FREECAD ASSEMBLY — COMPONENT RECIPES ("feeder_assembly")

This assembly document has 52 components, labeled P0..P51 below (a component is one placed body or linked part). 40 of them carry a construction recipe — the FreeCAD feature program that regenerates the part from scratch, quoted from this document or its linked companion documents; the rest are supplied as boundary geometry only. No exploded tour is included for this assembly.
NOTE — document 3 of 3 of this assembly tour. The two overview renders and the header above are repeated from document 1; the component sections below continue where the previous document stopped.
COMPONENT P31 — recipe-attached ("Body027", modeled in this document).
Construction recipe (the document's own serialized feature program — sketch geometry with constraints, then the solid features built on it; lengths are millimeters unless a unit is written):

FEATURE [Sketcher::SketchObject] Sketch136
  FullyConstrained = true
  MapMode = 5
  Support = -> [XY_Plane026]
  sketch-geometry (5):
    g0: LineSegment StartX=0 StartY=0 StartZ=0 EndX=65 EndY=0 EndZ=0
    g1: LineSegment StartX=65 StartY=0 StartZ=0 EndX=65 EndY=4.27341 EndZ=0
    g2: ArcOfCircle CenterX=85 CenterY=75 CenterZ=0 NormalX=0 NormalY=0 NormalZ=1 AngleXU=0 Radius=73.5 StartAngle=3.80049 EndAngle=4.43681
    g3: LineSegment StartX=26.8859 StartY=30 StartZ=0 EndX=0 EndY=30 EndZ=0
    g4: LineSegment StartX=0 StartY=30 StartZ=0 EndX=0 EndY=0 EndZ=0
  constraints (16):
    c: Coincident(g0,g-1)
    c: PointOnObject(g0,g-1)
    c: Coincident(g1,g0)
    c: Vertical(g1)
    c: Coincident(g2,g1)
    c: Coincident(g3,g2)
    c: PointOnObject(g3,g-2)
    c: Horizontal(g3)
    c: Coincident(g4,g3)
    c: PointOnObject(g4,g-1)
    c: Vertical(g4)
    c: DistanceX(g2) = 85
    c: DistanceY(g2) = 75
    c: Diameter(g2) = 147
    c: DistanceX(g0,g0) = 65
    c: DistanceY(g3) = 30
FEATURE [PartDesign::Pad] Pad064
  Direction = (0,0,1)
  Length = 4
  Length2 = 10
  Profile = -> Sketch136
  ReferenceAxis = -> Sketch136 [N_Axis]
  Reversed = true
  Type = 0
FEATURE [Sketcher::SketchObject] Sketch137
  ExternalGeometry = -> [Pad064]
  FullyConstrained = true
  MapMode = 5
  Placement = pos=(0,0,0) rot=(1,0,0;1.5708rad)
  Support = -> [Pad064]
  sketch-geometry (4):
    g0: LineSegment StartX=65 StartY=-4 StartZ=0 EndX=0 EndY=-4 EndZ=0
    g1: LineSegment StartX=0 StartY=-4 StartZ=0 EndX=0 EndY=-20 EndZ=0
    g2: LineSegment StartX=0 StartY=-20 StartZ=0 EndX=65 EndY=-20 EndZ=0
    g3: LineSegment StartX=65 StartY=-20 StartZ=0 EndX=65 EndY=-4 EndZ=0
  constraints (11):
    c: Coincident(g0,g1)
    c: Coincident(g1,g2)
    c: Coincident(g2,g3)
    c: Coincident(g3,g0)
    c: Horizontal(g0)
    c: Horizontal(g2)
    c: Vertical(g1)
    c: Vertical(g3)
    c: Coincident(g0,g-3)
    c: PointOnObject(g1,g-2)
    c: DistanceY(g1) = -20
FEATURE [PartDesign::Pad] Pad065
  BaseFeature = -> Pad064
  Direction = (0,-1,2e-16)
  Length = 3
  Length2 = 10
  Profile = -> Sketch137
  ReferenceAxis = -> Sketch137 [N_Axis]
  Reversed = true
  Type = 0
FEATURE [Sketcher::SketchObject] Sketch138
  ExternalGeometry = -> [Pad065]
  FullyConstrained = true
  MapMode = 5
  Placement = pos=(0,0,0) rot=(0.57735,-0.57735,-0.57735;2.0944rad)
  Support = -> [Pad065]
  sketch-geometry (4):
    g0: LineSegment StartX=-30 StartY=-4 StartZ=0 EndX=-3 EndY=-4 EndZ=0
    g1: LineSegment StartX=-3 StartY=-4 StartZ=0 EndX=-3 EndY=-20 EndZ=0
    g2: LineSegment StartX=-3 StartY=-20 StartZ=0 EndX=-30 EndY=-20 EndZ=0
    g3: LineSegment StartX=-30 StartY=-20 StartZ=0 EndX=-30 EndY=-4 EndZ=0
  constraints (10):
    c: Coincident(g0,g1)
    c: Coincident(g1,g2)
    c: Coincident(g2,g3)
    c: Coincident(g3,g0)
    c: Horizontal(g0)
    c: Horizontal(g2)
    c: Vertical(g1)
    c: Vertical(g3)
    c: Coincident(g0,g-3)
    c: Coincident(g1,g-4)
FEATURE [PartDesign::Pad] Pad066
  BaseFeature = -> Pad065
  Direction = (-1,0,0)
  Length = 8
  Length2 = 10
  Profile = -> Sketch138
  ReferenceAxis = -> Sketch138 [N_Axis]
  Reversed = true
  Type = 0
FEATURE [Sketcher::SketchObject] Sketch139
  ExternalGeometry = -> [Pad066]
  FullyConstrained = true
  MapMode = 5
  Placement = pos=(8,0,0) rot=(0.57735,0.57735,0.57735;2.0944rad)
  Support = -> [Pad066]
  sketch-geometry (4):
    g0: ArcOfCircle CenterX=9 CenterY=-10 CenterZ=0 NormalX=0 NormalY=0 NormalZ=1 AngleXU=0 Radius=6 StartAngle=1.5708 EndAngle=4.71239
    g1: ArcOfCircle CenterX=21 CenterY=-10 CenterZ=0 NormalX=0 NormalY=0 NormalZ=1 AngleXU=0 Radius=6 StartAngle=4.71239 EndAngle=7.85398
    g2: LineSegment StartX=9 StartY=-16 StartZ=0 EndX=21 EndY=-16 EndZ=0
    g3: LineSegment StartX=21 StartY=-4 StartZ=0 EndX=9 EndY=-4 EndZ=0
  constraints (10):
    c: Tangent(g0,g2) = -1.5708
    c: Tangent(g2,g1) = -1.5708
    c: Tangent(g1,g3) = -1.5708
    c: Tangent(g3,g0) = -1.5708
    c: Equal(g0,g1)
    c: Horizontal(g2)
    c: Diameter(g1) = 12
    c: DistanceY(g-4,g0) = 10
    c: DistanceX(g1,g-3) = 9
    c: DistanceX(g0) = 9
FEATURE [PartDesign::Pocket] Pocket067
  BaseFeature = -> Pad066
  Direction = (-1,0,0)
  Length = 5
  Length2 = 5
  Profile = -> Sketch139
  ReferenceAxis = -> Sketch139 [N_Axis]
  Type = 0
FEATURE [PartDesign::Fillet] Fillet060
  Base = -> Pocket067 [Edge28]
  BaseFeature = -> Pocket067
  Radius = 1
  SupportTransform = false
  UseAllEdges = false
FEATURE [PartDesign::Fillet] Fillet061
  Base = -> Fillet060 [Edge48]
  BaseFeature = -> Fillet060
  Radius = 10
  SupportTransform = false
  UseAllEdges = false
FEATURE [PartDesign::Fillet] Fillet062
  Base = -> Fillet061 [Edge56]
  BaseFeature = -> Fillet061
  Radius = 3.5
  SupportTransform = false
  UseAllEdges = false
FEATURE [PartDesign::Fillet] Fillet063
  Base = -> Fillet062 [Edge32,Edge25,Edge47,Edge23,Edge26,Edge24,Edge1,Edge2,Edge20,Edge11]
  BaseFeature = -> Fillet062
  Radius = 1
  SupportTransform = false
  UseAllEdges = false
FEATURE [PartDesign::Fillet] Fillet064
  Base = -> Fillet063 [Face31,Face32,Face21]
  BaseFeature = -> Fillet063
  Radius = 1
  SupportTransform = false
  UseAllEdges = false
FEATURE [PartDesign::Fillet] Fillet065
  Base = -> Fillet064 [Face33]
  BaseFeature = -> Fillet064
  Radius = 0.5
  SupportTransform = false
  UseAllEdges = false
FEATURE [PartDesign::Fillet] Fillet066
  Base = -> Fillet065 [Face23]
  BaseFeature = -> Fillet065
  Radius = 0.9
  SupportTransform = false
  UseAllEdges = false
FEATURE [Sketcher::SketchObject] Sketch140
  ExternalGeometry = -> [Fillet066]
  FullyConstrained = true
  MapMode = 5
  Placement = pos=(3,0,0) rot=(0.57735,0.57735,0.57735;2.0944rad)
  Support = -> [Fillet066]
  sketch-geometry (2):
    g0: Circle CenterX=9 CenterY=-10 CenterZ=0 NormalX=0 NormalY=0 NormalZ=1 AngleXU=0 Radius=2.075
    g1: Circle CenterX=21 CenterY=-10 CenterZ=0 NormalX=0 NormalY=0 NormalZ=1 AngleXU=0 Radius=2.075
  constraints (4):
    c: Coincident(g0,g-3)
    c: Coincident(g1,g-4)
    c: Equal(g0,g1)
    c: Diameter(g1) = 4.15
FEATURE [PartDesign::Pocket] Pocket068
  BaseFeature = -> Fillet066
  Direction = (-1,0,0)
  Length = 5
  Length2 = 5
  Profile = -> Sketch140
  ReferenceAxis = -> Sketch140 [N_Axis]
  Type = 0
FEATURE [Sketcher::SketchObject] Sketch141
  ExternalGeometry = -> [Pocket068]
  FullyConstrained = true
  MapMode = 5
  Placement = pos=(0,3,-7e-16) rot=(0,0.707107,0.707107;3.14159rad)
  Support = -> [Pocket068]
  sketch-geometry (4):
    g0: LineSegment StartX=-8 StartY=-18.5 StartZ=0 EndX=-38 EndY=-18.5 EndZ=0
    g1: LineSegment StartX=-38 StartY=-18.5 StartZ=0 EndX=-38 EndY=-16.5 EndZ=0
    g2: LineSegment StartX=-38 StartY=-16.5 StartZ=0 EndX=-8 EndY=-16.5 EndZ=0
    g3: LineSegment StartX=-8 StartY=-16.5 StartZ=0 EndX=-8 EndY=-18.5 EndZ=0
  constraints (12):
    c: Coincident(g0,g1)
    c: Coincident(g1,g2)
    c: Coincident(g2,g3)
    c: Coincident(g3,g0)
    c: Horizontal(g0)
    c: Horizontal(g2)
    c: Vertical(g1)
    c: Vertical(g3)
    c: DistanceY(g3,g3) = 2
    c: DistanceX(g0,g0) = 30
    c: PointOnObject(g0,g-3)
    c: DistanceY(g-3,g0) = 0.5
FEATURE [PartDesign::Pad] Pad067
  BaseFeature = -> Pocket068
  Direction = (0,1,-2e-16)
  Length = 5
  Length2 = 10
  Profile = -> Sketch141
  ReferenceAxis = -> Sketch141 [N_Axis]
  Type = 0
FEATURE [Sketcher::SketchObject] Sketch142
  ExternalGeometry = -> [Pad067]
  FullyConstrained = true
  MapMode = 5
  Placement = pos=(0,-4.1e-15,-18.5) rot=(1,0,0;3.14159rad)
  Support = -> [Pad067]
  sketch-geometry (3):
    g0: LineSegment StartX=8 StartY=-8 StartZ=0 EndX=38 EndY=-3 EndZ=0
    g1: LineSegment StartX=38 StartY=-3 StartZ=0 EndX=38 EndY=-8 EndZ=0
    g2: LineSegment StartX=38 StartY=-8 StartZ=0 EndX=8 EndY=-8 EndZ=0
  constraints (6):
    c: Coincident(g0,g-6)
    c: Coincident(g0,g-5)
    c: Coincident(g1,g0)
    c: Coincident(g1,g-5)
    c: Coincident(g2,g1)
    c: Coincident(g2,g0)
FEATURE [PartDesign::Pocket] Pocket069
  BaseFeature = -> Pad067
  Direction = (0,2e-16,1)
  Length = 0
  Length2 = 5
  Profile = -> Sketch142
  ReferenceAxis = -> Sketch142 [N_Axis]
  Type = 2
FEATURE [PartDesign::Fillet] Fillet067
  Base = -> Pocket069 [Face26,Face27,Face24]
  BaseFeature = -> Pocket069
  Radius = 0.4
  SupportTransform = false
  UseAllEdges = false
FEATURE [PartDesign::Fillet] Fillet068
  Base = -> Fillet067 [Face69,Face68]
  BaseFeature = -> Fillet067
  Radius = 0.3
  SupportTransform = false
  UseAllEdges = false
FEATURE [PartDesign::Body] Body027
  Group = -> [Sketch136,Pad064,Sketch137,Pad065,Sketch138,Pad066,Sketch139,Pocket067,Fillet060,Fillet061,Fillet062,Fillet063,Fillet064,Fillet065,Fillet066,Sketch140,Pocket068,Sketch141,Pad067,Sketch142,Pocket069,Fillet067,Fillet068]
  Origin = -> Origin026
  Tip = -> Fillet068
COMPONENT P32 — recipe-attached ("Body029", modeled in this document).
Construction recipe (the document's own serialized feature program — sketch geometry with constraints, then the solid features built on it; lengths are millimeters unless a unit is written):

FEATURE [Sketcher::SketchObject] Sketch144
  FullyConstrained = true
  MapMode = 5
  Support = -> [XY_Plane028]
  sketch-geometry (4):
    g0: LineSegment StartX=0 StartY=0 StartZ=0 EndX=65.5 EndY=0 EndZ=0
    g1: LineSegment StartX=65.5 StartY=0 StartZ=0 EndX=65.5 EndY=30.6 EndZ=0
    g2: LineSegment StartX=65.5 StartY=30.6 StartZ=0 EndX=0 EndY=30.6 EndZ=0
    g3: LineSegment StartX=0 StartY=30.6 StartZ=0 EndX=0 EndY=0 EndZ=0
  constraints (11):
    c: Coincident(g0,g1)
    c: Coincident(g1,g2)
    c: Coincident(g2,g3)
    c: Coincident(g3,g0)
    c: Horizontal(g0)
    c: Horizontal(g2)
    c: Vertical(g1)
    c: Vertical(g3)
    c: Coincident(g0,g-1)
    c: DistanceX(g0,g0) = 65.5
    c: DistanceY(g1,g1) = 30.6
FEATURE [PartDesign::Pad] Pad069
  Direction = (0,0,1)
  Length = 1.6
  Length2 = 10
  Profile = -> Sketch144
  ReferenceAxis = -> Sketch144 [N_Axis]
  Type = 0
FEATURE [Sketcher::SketchObject] Sketch145
  ExternalGeometry = -> [Pad069]
  FullyConstrained = true
  MapMode = 5
  Placement = pos=(0,0,1.6) rot=(0,0,1;0rad)
  Support = -> [Pad069]
  sketch-geometry (4):
    g0: Circle CenterX=3.5 CenterY=26.5 CenterZ=0 NormalX=0 NormalY=0 NormalZ=1 AngleXU=0 Radius=1.5
    g1: Circle CenterX=3.5 CenterY=3.5 CenterZ=0 NormalX=0 NormalY=0 NormalZ=1 AngleXU=0 Radius=1.5
    g2: Circle CenterX=61.5 CenterY=3.5 CenterZ=0 NormalX=0 NormalY=0 NormalZ=1 AngleXU=0 Radius=1.5
    g3: Circle CenterX=61.5 CenterY=26.5 CenterZ=0 NormalX=0 NormalY=0 NormalZ=1 AngleXU=0 Radius=1.5
  constraints (12):
    c: Equal(g2,g3)
    c: Equal(g3,g0)
    c: Equal(g0,g1)
    c: Diameter(g2) = 3
    c: Horizontal(g1,g2)
    c: Horizontal(g3,g0)
    c: Vertical(g3,g2)
    c: Vertical(g0,g1)
    c: DistanceX(g1) = 3.5
    c: DistanceY(g1) = 3.5
    c: DistanceX(g1,g2) = 58
    c: DistanceY(g1,g0) = 23
FEATURE [PartDesign::Pocket] Pocket070
  BaseFeature = -> Pad069
  Direction = (0,0,-1)
  Length = 5
  Length2 = 5
  Profile = -> Sketch145
  ReferenceAxis = -> Sketch145 [N_Axis]
  Type = 0
FEATURE [Sketcher::SketchObject] Sketch146
  ExternalGeometry = -> [Pocket070]
  FullyConstrained = true
  MapMode = 5
  Placement = pos=(0,0,0) rot=(1,0,0;3.14159rad)
  Support = -> [Pocket070]
  sketch-geometry (6):
    g0: LineSegment StartX=6.875 StartY=-29 StartZ=0 EndX=58.125 EndY=-29 EndZ=0
    g1: LineSegment StartX=58.125 StartY=-29 StartZ=0 EndX=58.125 EndY=-24 EndZ=0
    g2: LineSegment StartX=58.125 StartY=-24 StartZ=0 EndX=6.875 EndY=-24 EndZ=0
    g3: LineSegment StartX=6.875 StartY=-24 StartZ=0 EndX=6.875 EndY=-29 EndZ=0
    g4: GeomPoint X=32.5 Y=-29 Z=0
    g5: GeomPoint X=6.875 Y=-26.5 Z=0
  constraints (14):
    c: Coincident(g0,g1)
    c: Coincident(g1,g2)
    c: Coincident(g2,g3)
    c: Coincident(g3,g0)
    c: Horizontal(g0)
    c: Horizontal(g2)
    c: Vertical(g1)
    c: Vertical(g3)
    c: DistanceX(g0,g0) = 51.25
    c: DistanceY(g3,g3) = 5
    c: Symmetric(g0,g0,g4)
    c: DistanceX(g-4,g4) = 29
    c: Symmetric(g3,g3,g5)
    c: Horizontal(g5,g-4)
FEATURE [PartDesign::Pad] Pad070
  BaseFeature = -> Pocket070
  Direction = (0,0,-1)
  Length = 30
  Length2 = 10
  Profile = -> Sketch146
  ReferenceAxis = -> Sketch146 [N_Axis]
  Type = 0
FEATURE [Sketcher::SketchObject] Sketch147
  ExternalGeometry = -> [Pad070]
  FullyConstrained = true
  MapMode = 5
  Placement = pos=(0,0,1.6) rot=(0,0,1;0rad)
  Support = -> [Pad070]
  sketch-geometry (10):
    g0: LineSegment StartX=6.5 StartY=30.6 StartZ=0 EndX=58.5 EndY=30.6 EndZ=0
    g1: LineSegment StartX=58.5 StartY=30.6 StartZ=0 EndX=58.5 EndY=24.1 EndZ=0
    g2: LineSegment StartX=58.5 StartY=24.1 StartZ=0 EndX=6.5 EndY=24.1 EndZ=0
    g3: LineSegment StartX=6.5 StartY=24.1 StartZ=0 EndX=6.5 EndY=30.6 EndZ=0
    g4: LineSegment StartX=8.5 StartY=0 StartZ=0 EndX=56.5 EndY=0 EndZ=0
    g5: LineSegment StartX=56.5 StartY=0 StartZ=0 EndX=56.5 EndY=8.5 EndZ=0
    g6: LineSegment StartX=56.5 StartY=8.5 StartZ=0 EndX=8.5 EndY=8.5 EndZ=0
    g7: LineSegment StartX=8.5 StartY=8.5 StartZ=0 EndX=8.5 EndY=0 EndZ=0
    g8: GeomPoint X=32.5 Y=8.5 Z=0
    g9: GeomPoint X=32.5 Y=24.1 Z=0
  constraints (26):
    c: Coincident(g0,g1)
    c: Coincident(g1,g2)
    c: Coincident(g2,g3)
    c: Coincident(g3,g0)
    c: Horizontal(g0)
    c: Horizontal(g2)
    c: Vertical(g1)
    c: Vertical(g3)
    c: PointOnObject(g0,g-3)
    c: Coincident(g4,g5)
    c: Coincident(g5,g6)
    c: Coincident(g6,g7)
    c: Coincident(g7,g4)
    c: Horizontal(g4)
    c: Horizontal(g6)
    c: Vertical(g5)
    c: Vertical(g7)
    c: PointOnObject(g4,g-1)
    c: DistanceY(g5,g5) = 8.5
    c: DistanceX(g4,g4) = 48
    c: DistanceX(g2,g2) = 52
    c: DistanceY(g1,g1) = 6.5
    c: Symmetric(g6,g6,g8)
    c: Symmetric(g2,g2,g9)
    c: Vertical(g9,g8)
    c: DistanceX(g-4,g9) = 29
FEATURE [PartDesign::Pad] Pad071
  BaseFeature = -> Pad070
  Direction = (0,0,1)
  Length = 20
  Length2 = 10
  Profile = -> Sketch147
  ReferenceAxis = -> Sketch147 [N_Axis]
  Type = 0
FEATURE [Sketcher::SketchObject] Sketch148
  FullyConstrained = true
  MapMode = 5
  Placement = pos=(0,0,1.6) rot=(0,0,1;0rad)
  Support = -> [Pad071]
  sketch-geometry (4):
    g0: LineSegment StartX=0 StartY=11.5 StartZ=0 EndX=7.5 EndY=11.5 EndZ=0
    g1: LineSegment StartX=7.5 StartY=11.5 StartZ=0 EndX=7.5 EndY=18.5 EndZ=0
    g2: LineSegment StartX=7.5 StartY=18.5 StartZ=0 EndX=0 EndY=18.5 EndZ=0
    g3: LineSegment StartX=0 StartY=18.5 StartZ=0 EndX=0 EndY=11.5 EndZ=0
  constraints (12):
    c: Coincident(g0,g1)
    c: Coincident(g1,g2)
    c: Coincident(g2,g3)
    c: Coincident(g3,g0)
    c: Horizontal(g0)
    c: Horizontal(g2)
    c: Vertical(g1)
    c: Vertical(g3)
    c: PointOnObject(g0,g-2)
    c: DistanceY(g0) = 11.5
    c: DistanceY(g1,g1) = 7
    c: DistanceX(g0,g0) = 7.5
FEATURE [PartDesign::Pad] Pad072
  BaseFeature = -> Pad071
  Direction = (0,0,1)
  Length = 9.5
  Length2 = 10
  Profile = -> Sketch148
  ReferenceAxis = -> Sketch148 [N_Axis]
  Type = 0
FEATURE [PartDesign::Body] Body029
  Group = -> [Sketch144,Pad069,Sketch145,Pocket070,Sketch146,Pad070,Sketch147,Pad071,Sketch148,Pad072]
  Origin = -> Origin028
  Tip = -> Pad072
COMPONENT P33 — recipe-attached ("Body030", modeled in this document).
Construction recipe (the document's own serialized feature program — sketch geometry with constraints, then the solid features built on it; lengths are millimeters unless a unit is written):

FEATURE [Sketcher::SketchObject] Sketch149
  FullyConstrained = true
  MapMode = 5
  Support = -> [XY_Plane029]
  sketch-geometry (4):
    g0: LineSegment StartX=0 StartY=0 StartZ=0 EndX=85 EndY=0 EndZ=0
    g1: LineSegment StartX=85 StartY=0 StartZ=0 EndX=85 EndY=56 EndZ=0
    g2: LineSegment StartX=85 StartY=56 StartZ=0 EndX=0 EndY=56 EndZ=0
    g3: LineSegment StartX=0 StartY=56 StartZ=0 EndX=0 EndY=0 EndZ=0
  constraints (11):
    c: Coincident(g0,g1)
    c: Coincident(g1,g2)
    c: Coincident(g2,g3)
    c: Coincident(g3,g0)
    c: Horizontal(g0)
    c: Horizontal(g2)
    c: Vertical(g1)
    c: Vertical(g3)
    c: Coincident(g0,g-1)
    c: DistanceX(g0,g0) = 85
    c: DistanceY(g3,g3) = 56
FEATURE [PartDesign::Pad] Pad073
  Direction = (0,0,1)
  Length = 1.5
  Length2 = 10
  Profile = -> Sketch149
  ReferenceAxis = -> Sketch149 [N_Axis]
  Type = 0
FEATURE [Sketcher::SketchObject] Sketch150
  ExternalGeometry = -> [Pad073]
  FullyConstrained = true
  MapMode = 5
  Placement = pos=(0,0,1.5) rot=(0,0,1;0rad)
  Support = -> [Pad073]
  sketch-geometry (4):
    g0: Circle CenterX=3.5 CenterY=52.5 CenterZ=0 NormalX=0 NormalY=0 NormalZ=1 AngleXU=0 Radius=1.375
    g1: Circle CenterX=61.5 CenterY=52.5 CenterZ=0 NormalX=0 NormalY=0 NormalZ=1 AngleXU=0 Radius=1.375
    g2: Circle CenterX=3.5 CenterY=3.5 CenterZ=0 NormalX=0 NormalY=0 NormalZ=1 AngleXU=0 Radius=1.375
    g3: Circle CenterX=61.5 CenterY=3.5 CenterZ=0 NormalX=0 NormalY=0 NormalZ=1 AngleXU=0 Radius=1.375
  constraints (12):
    c: Equal(g0,g1)
    c: Equal(g1,g2)
    c: Equal(g2,g3)
    c: Diameter(g1) = 2.75
    c: Vertical(g0,g2)
    c: DistanceX(g2) = 3.5
    c: DistanceY(g2) = 3.5
    c: DistanceY(g0,g-3) = 3.5
    c: Horizontal(g3,g2)
    c: Horizontal(g1,g0)
    c: DistanceX(g0,g1) = 58
    c: Vertical(g3,g1)
FEATURE [PartDesign::Pocket] Pocket071
  BaseFeature = -> Pad073
  Direction = (0,0,-1)
  Length = 5
  Length2 = 5
  Profile = -> Sketch150
  ReferenceAxis = -> Sketch150 [N_Axis]
  Type = 0
FEATURE [Sketcher::SketchObject] Sketch151
  FullyConstrained = true
  MapMode = 5
  Placement = pos=(0,0,1.5) rot=(0,0,1;0rad)
  Support = -> [Pocket071]
  sketch-geometry (5):
    g0: LineSegment StartX=24.5 StartY=-1.5 StartZ=0 EndX=39.5 EndY=-1.5 EndZ=0
    g1: LineSegment StartX=39.5 StartY=-1.5 StartZ=0 EndX=39.5 EndY=10 EndZ=0
    g2: LineSegment StartX=39.5 StartY=10 StartZ=0 EndX=24.5 EndY=10 EndZ=0
    g3: LineSegment StartX=24.5 StartY=10 StartZ=0 EndX=24.5 EndY=-1.5 EndZ=0
    g4: GeomPoint X=32 Y=-1.5 Z=0
  constraints (13):
    c: Coincident(g0,g1)
    c: Coincident(g1,g2)
    c: Coincident(g2,g3)
    c: Coincident(g3,g0)
    c: Horizontal(g0)
    c: Horizontal(g2)
    c: Vertical(g1)
    c: Vertical(g3)
    c: DistanceX(g0,g0) = 15
    c: DistanceY(g1,g1) = 11.5
    c: DistanceY(g0) = -1.5
    c: Symmetric(g0,g0,g4)
    c: DistanceX(g4) = 32
FEATURE [PartDesign::Pad] Pad074
  BaseFeature = -> Pocket071
  Direction = (0,0,1)
  Length = 6.5
  Length2 = 0.5
  Profile = -> Sketch151
  ReferenceAxis = -> Sketch151 [N_Axis]
  Type = 0
FEATURE [Sketcher::SketchObject] Sketch152
  ExternalGeometry = -> [Pad074]
  FullyConstrained = true
  MapMode = 5
  Placement = pos=(0,0,1.5) rot=(0,0,1;0rad)
  Support = -> [Pad074]
  sketch-geometry (10):
    g0: LineSegment StartX=69.5 StartY=21.5 StartZ=0 EndX=87 EndY=21.5 EndZ=0
    g1: LineSegment StartX=87 StartY=21.5 StartZ=0 EndX=87 EndY=36.5 EndZ=0
    g2: LineSegment StartX=87 StartY=36.5 StartZ=0 EndX=69.5 EndY=36.5 EndZ=0
    g3: LineSegment StartX=69.5 StartY=36.5 StartZ=0 EndX=69.5 EndY=21.5 EndZ=0
    g4: LineSegment StartX=69.5 StartY=39.5 StartZ=0 EndX=87 EndY=39.5 EndZ=0
    g5: LineSegment StartX=87 StartY=39.5 StartZ=0 EndX=87 EndY=54.5 EndZ=0
    g6: LineSegment StartX=87 StartY=54.5 StartZ=0 EndX=69.5 EndY=54.5 EndZ=0
    g7: LineSegment StartX=69.5 StartY=54.5 StartZ=0 EndX=69.5 EndY=39.5 EndZ=0
    g8: GeomPoint X=87 Y=29 Z=0
    g9: GeomPoint X=87 Y=47 Z=0
  constraints (26):
    c: Coincident(g0,g1)
    c: Coincident(g1,g2)
    c: Coincident(g2,g3)
    c: Coincident(g3,g0)
    c: Horizontal(g0)
    c: Horizontal(g2)
    c: Vertical(g1)
    c: Vertical(g3)
    c: Coincident(g4,g5)
    c: Coincident(g5,g6)
    c: Coincident(g6,g7)
    c: Coincident(g7,g4)
    c: Horizontal(g4)
    c: Horizontal(g6)
    c: Vertical(g5)
    c: Vertical(g7)
    c: Equal(g5,g1)
    c: Equal(g0,g4)
    c: Vertical(g0,g4)
    c: Symmetric(g5,g5,g9)
    c: Symmetric(g1,g1,g8)
    c: DistanceY(g5,g5) = 15
    c: DistanceY(g9) = 47
    c: DistanceY(g8) = 29
    c: DistanceX(g-3,g0) = 2
    c: DistanceX(g0,g0) = 17.5
FEATURE [PartDesign::Pad] Pad075
  BaseFeature = -> Pad074
  Direction = (0,0,1)
  Length = 16
  Length2 = 10
  Profile = -> Sketch152
  ReferenceAxis = -> Sketch152 [N_Axis]
  Type = 0
FEATURE [Sketcher::SketchObject] Sketch153
  ExternalGeometry = -> [Pad075]
  FullyConstrained = true
  MapMode = 5
  Placement = pos=(0,0,1.5) rot=(0,0,1;0rad)
  Support = -> [Pad075]
  sketch-geometry (5):
    g0: LineSegment StartX=65.5 StartY=2.25 StartZ=0 EndX=87 EndY=2.25 EndZ=0
    g1: LineSegment StartX=87 StartY=2.25 StartZ=0 EndX=87 EndY=18.25 EndZ=0
    g2: LineSegment StartX=87 StartY=18.25 StartZ=0 EndX=65.5 EndY=18.25 EndZ=0
    g3: LineSegment StartX=65.5 StartY=18.25 StartZ=0 EndX=65.5 EndY=2.25 EndZ=0
    g4: GeomPoint X=87 Y=10.25 Z=0
  constraints (13):
    c: Coincident(g0,g1)
    c: Coincident(g1,g2)
    c: Coincident(g2,g3)
    c: Coincident(g3,g0)
    c: Horizontal(g0)
    c: Horizontal(g2)
    c: Vertical(g1)
    c: Vertical(g3)
    c: DistanceY(g1,g1) = 16
    c: DistanceX(g0,g0) = 21.5
    c: DistanceX(g-3,g0) = 2
    c: Symmetric(g1,g1,g4)
    c: DistanceY(g4) = 10.25
FEATURE [PartDesign::Pad] Pad076
  BaseFeature = -> Pad075
  Direction = (0,0,1)
  Length = 13.5
  Length2 = 10
  Profile = -> Sketch153
  ReferenceAxis = -> Sketch153 [N_Axis]
  Type = 0
FEATURE [Sketcher::SketchObject] Sketch154
  ExternalGeometry = -> [Pad076]
  FullyConstrained = true
  MapMode = 5
  Placement = pos=(0,0,1.5) rot=(0,0,1;0rad)
  Support = -> [Pad076]
  sketch-geometry (6):
    g0: LineSegment StartX=7.5 StartY=50 StartZ=0 EndX=57.5 EndY=50 EndZ=0
    g1: LineSegment StartX=57.5 StartY=50 StartZ=0 EndX=57.5 EndY=55 EndZ=0
    g2: LineSegment StartX=57.5 StartY=55 StartZ=0 EndX=7.5 EndY=55 EndZ=0
    g3: LineSegment StartX=7.5 StartY=55 StartZ=0 EndX=7.5 EndY=50 EndZ=0
    g4: GeomPoint X=32.5 Y=55 Z=0
    g5: GeomPoint X=7.5 Y=52.5 Z=0
  constraints (14):
    c: Coincident(g0,g1)
    c: Coincident(g1,g2)
    c: Coincident(g2,g3)
    c: Coincident(g3,g0)
    c: Horizontal(g0)
    c: Horizontal(g2)
    c: Vertical(g1)
    c: Vertical(g3)
    c: Symmetric(g2,g2,g4)
    c: DistanceX(g-3,g4) = 29
    c: DistanceY(g3,g3) = 5
    c: DistanceX(g0,g0) = 50
    c: Symmetric(g3,g3,g5)
    c: Horizontal(g5,g-3)
FEATURE [PartDesign::Pad] Pad077
  BaseFeature = -> Pad076
  Direction = (0,0,1)
  Length = 30
  Length2 = 10
  Profile = -> Sketch154
  ReferenceAxis = -> Sketch154 [N_Axis]
  Type = 0
FEATURE [Sketcher::SketchObject] Sketch155
  FullyConstrained = true
  MapMode = 5
  Placement = pos=(0,0,1.5) rot=(0,0,1;0rad)
  Support = -> [Pad077]
  sketch-geometry (5):
    g0: LineSegment StartX=6.6 StartY=4.5 StartZ=0 EndX=14.6 EndY=4.5 EndZ=0
    g1: LineSegment StartX=14.6 StartY=4.5 StartZ=0 EndX=14.6 EndY=-1.5 EndZ=0
    g2: LineSegment StartX=14.6 StartY=-1.5 StartZ=0 EndX=6.6 EndY=-1.5 EndZ=0
    g3: LineSegment StartX=6.6 StartY=-1.5 StartZ=0 EndX=6.6 EndY=4.5 EndZ=0
    g4: GeomPoint X=10.6 Y=-1.5 Z=0
  constraints (13):
    c: Coincident(g0,g1)
    c: Coincident(g1,g2)
    c: Coincident(g2,g3)
    c: Coincident(g3,g0)
    c: Horizontal(g0)
    c: Horizontal(g2)
    c: Vertical(g1)
    c: Vertical(g3)
    c: DistanceX(g2,g2) = 8
    c: DistanceY(g3,g3) = 6
    c: DistanceY(g2) = -1.5
    c: Symmetric(g2,g2,g4)
    c: DistanceX(g4) = 10.6
FEATURE [PartDesign::Pad] Pad078
  BaseFeature = -> Pad077
  Direction = (0,0,1)
  Length = 3
  Length2 = 0.5
  Profile = -> Sketch155
  ReferenceAxis = -> Sketch155 [N_Axis]
  Type = 4
FEATURE [Sketcher::SketchObject] Sketch156
  FullyConstrained = true
  MapMode = 5
  Placement = pos=(0,0,1.5) rot=(0,0,1;0rad)
  Support = -> [Pad078]
  sketch-geometry (5):
    g0: LineSegment StartX=49.875 StartY=12.5 StartZ=0 EndX=57.125 EndY=12.5 EndZ=0
    g1: LineSegment StartX=57.125 StartY=12.5 StartZ=0 EndX=57.125 EndY=-2.5 EndZ=0
    g2: LineSegment StartX=57.125 StartY=-2.5 StartZ=0 EndX=49.875 EndY=-2.5 EndZ=0
    g3: LineSegment StartX=49.875 StartY=-2.5 StartZ=0 EndX=49.875 EndY=12.5 EndZ=0
    g4: GeomPoint X=53.5 Y=-2.5 Z=0
  constraints (13):
    c: Coincident(g0,g1)
    c: Coincident(g1,g2)
    c: Coincident(g2,g3)
    c: Coincident(g3,g0)
    c: Horizontal(g0)
    c: Horizontal(g2)
    c: Vertical(g1)
    c: Vertical(g3)
    c: DistanceX(g2,g2) = 7.25
    c: Symmetric(g2,g2,g4)
    c: DistanceX(g4) = 53.5
    c: DistanceY(g1,g1) = 15
    c: DistanceY(g4) = -2.5
FEATURE [PartDesign::Pad] Pad079
  BaseFeature = -> Pad078
  Direction = (0,0,1)
  Length = 6
  Length2 = 10
  Profile = -> Sketch156
  ReferenceAxis = -> Sketch156 [N_Axis]
  Type = 0
FEATURE [Sketcher::SketchObject] Sketch157
  FullyConstrained = true
  MapMode = 5
  Placement = pos=(0,0,0) rot=(1,0,0;3.14159rad)
  Support = -> [Pad079]
  sketch-geometry (4):
    g0: LineSegment StartX=-3 StartY=-22 StartZ=0 EndX=12.8 EndY=-22 EndZ=0
    g1: LineSegment StartX=12.8 StartY=-22 StartZ=0 EndX=12.8 EndY=-34 EndZ=0
    g2: LineSegment StartX=12.8 StartY=-34 StartZ=0 EndX=-3 EndY=-34 EndZ=0
    g3: LineSegment StartX=-3 StartY=-34 StartZ=0 EndX=-3 EndY=-22 EndZ=0
  constraints (12):
    c: Coincident(g0,g1)
    c: Coincident(g1,g2)
    c: Coincident(g2,g3)
    c: Coincident(g3,g0)
    c: Horizontal(g0)
    c: Horizontal(g2)
    c: Vertical(g1)
    c: Vertical(g3)
    c: DistanceX(g2,g2) = 15.8
    c: DistanceY(g1,g1) = 12
    c: DistanceY(g0) = -22
    c: DistanceX(g0) = -3
FEATURE [PartDesign::Pad] Pad080
  BaseFeature = -> Pad079
  Direction = (0,0,-1)
  Length = 1.5
  Length2 = 10
  Profile = -> Sketch157
  ReferenceAxis = -> Sketch157 [N_Axis]
  Type = 0
FEATURE [Sketcher::SketchObject] Sketch158
  FullyConstrained = true
  MapMode = 5
  Placement = pos=(0,0,0) rot=(1,0,0;3.14159rad)
  Support = -> [Pad080]
  sketch-geometry (4):
    g0: LineSegment StartX=17 StartY=-10 StartZ=0 EndX=82 EndY=-10 EndZ=0
    g1: LineSegment StartX=82 StartY=-10 StartZ=0 EndX=82 EndY=-45 EndZ=0
    g2: LineSegment StartX=82 StartY=-45 StartZ=0 EndX=17 EndY=-45 EndZ=0
    g3: LineSegment StartX=17 StartY=-45 StartZ=0 EndX=17 EndY=-10 EndZ=0
  constraints (12):
    c: Coincident(g0,g1)
    c: Coincident(g1,g2)
    c: Coincident(g2,g3)
    c: Coincident(g3,g0)
    c: Horizontal(g0)
    c: Horizontal(g2)
    c: Vertical(g1)
    c: Vertical(g3)
    c: DistanceX(g0) = 17
    c: DistanceY(g0) = -10
    c: DistanceY(g1,g1) = 35
    c: DistanceX(g2,g2) = 65
FEATURE [PartDesign::Pad] Pad081
  BaseFeature = -> Pad080
  Direction = (0,0,-1)
  Length = 2.2
  Length2 = 10
  Profile = -> Sketch158
  ReferenceAxis = -> Sketch158 [N_Axis]
  Type = 0
FEATURE [PartDesign::Body] Body030
  Group = -> [Sketch149,Pad073,Sketch150,Pocket071,Sketch151,Pad074,Sketch152,Pad075,Sketch153,Pad076,Sketch154,Pad077,Sketch155,Pad078,Sketch156,Pad079,Sketch157,Pad080,Sketch158,Pad081]
  Origin = -> Origin029
  Tip = -> Pad081
COMPONENT P34 — recipe-attached ("Body031", modeled in this document).
Construction recipe (the document's own serialized feature program — sketch geometry with constraints, then the solid features built on it; lengths are millimeters unless a unit is written):

FEATURE [Sketcher::SketchObject] Sketch159
  FullyConstrained = true
  MapMode = 5
  Support = -> [XY_Plane030]
  sketch-geometry (4):
    g0: LineSegment StartX=0 StartY=0 StartZ=0 EndX=110 EndY=0 EndZ=0
    g1: LineSegment StartX=110 StartY=0 StartZ=0 EndX=110 EndY=73 EndZ=0
    g2: LineSegment StartX=110 StartY=73 StartZ=0 EndX=0 EndY=73 EndZ=0
    g3: LineSegment StartX=0 StartY=73 StartZ=0 EndX=0 EndY=0 EndZ=0
  constraints (11):
    c: Coincident(g0,g1)
    c: Coincident(g1,g2)
    c: Coincident(g2,g3)
    c: Coincident(g3,g0)
    c: Horizontal(g0)
    c: Horizontal(g2)
    c: Vertical(g1)
    c: Vertical(g3)
    c: Coincident(g0,g-1)
    c: DistanceY(g1,g1) = 73
    c: DistanceX(g0,g0) = 110
FEATURE [PartDesign::Pad] Pad082
  Direction = (0,0,1)
  Length = 37
  Length2 = 10
  Profile = -> Sketch159
  ReferenceAxis = -> Sketch159 [N_Axis]
  Type = 0
FEATURE [PartDesign::Thickness] Thickness
  Base = -> Pad082 [Face6]
  BaseFeature = -> Pad082
  Intersection = false
  Join = 0
  Mode = 0
  Reversed = true
  SupportTransform = false
  Value = 2.5
FEATURE [PartDesign::Body] Body031
  Group = -> [Sketch159,Pad082,Thickness]
  Origin = -> Origin030
  Tip = -> Thickness
COMPONENT P35 — recipe-attached ("Body032", modeled in this document).
Construction recipe (the document's own serialized feature program — sketch geometry with constraints, then the solid features built on it; lengths are millimeters unless a unit is written):

FEATURE [Sketcher::SketchObject] Sketch161
  FullyConstrained = true
  MapMode = 5
  Support = -> [XY_Plane031]
  sketch-geometry (4):
    g0: LineSegment StartX=0 StartY=0 StartZ=0 EndX=120 EndY=0 EndZ=0
    g1: LineSegment StartX=120 StartY=0 StartZ=0 EndX=120 EndY=73 EndZ=0
    g2: LineSegment StartX=120 StartY=73 StartZ=0 EndX=0 EndY=73 EndZ=0
    g3: LineSegment StartX=0 StartY=73 StartZ=0 EndX=0 EndY=0 EndZ=0
  constraints (11):
    c: Coincident(g0,g1)
    c: Coincident(g1,g2)
    c: Coincident(g2,g3)
    c: Coincident(g3,g0)
    c: Horizontal(g0)
    c: Horizontal(g2)
    c: Vertical(g1)
    c: Vertical(g3)
    c: Coincident(g0,g-1)
    c: DistanceY(g1,g1) = 73
    c: DistanceX(g0,g0) = 120
FEATURE [PartDesign::Pad] Pad084
  Direction = (0,0,1)
  Length = 2.5
  Length2 = 10
  Profile = -> Sketch161
  ReferenceAxis = -> Sketch161 [N_Axis]
  Type = 0
FEATURE [Sketcher::SketchObject] Sketch163
  ExternalGeometry = -> [Pad084]
  FullyConstrained = true
  MapMode = 5
  Placement = pos=(0,0,0) rot=(1,0,0;3.14159rad)
  Support = -> [Pad084]
  sketch-geometry (6):
    g0: LineSegment StartX=0 StartY=0 StartZ=0 EndX=120 EndY=0 EndZ=0
    g1: LineSegment StartX=120 StartY=0 StartZ=0 EndX=120 EndY=-64.9 EndZ=0
    g2: LineSegment StartX=120 StartY=-64.9 StartZ=0 EndX=117.5 EndY=-64.9 EndZ=0
    g3: LineSegment StartX=117.5 StartY=-64.9 StartZ=0 EndX=117.5 EndY=-2.5 EndZ=0
    g4: LineSegment StartX=117.5 StartY=-2.5 StartZ=0 EndX=0 EndY=-2.5 EndZ=0
    g5: LineSegment StartX=0 StartY=-2.5 StartZ=0 EndX=0 EndY=0 EndZ=0
  constraints (16):
    c: Coincident(g0,g-5)
    c: Coincident(g0,g-4)
    c: Coincident(g1,g0)
    c: PointOnObject(g1,g-4)
    c: Coincident(g2,g1)
    c: Horizontal(g2)
    c: Coincident(g3,g2)
    c: Vertical(g3)
    c: Coincident(g4,g3)
    c: PointOnObject(g4,g-5)
    c: Horizontal(g4)
    c: Coincident(g5,g4)
    c: Coincident(g5,g0)
    c: DistanceY(g5,g5) = 2.5
    c: DistanceX(g2,g2) = 2.5
    c: DistanceY(g-4,g1) = 8.1
FEATURE [PartDesign::Pad] Pad086
  BaseFeature = -> Pad084
  Direction = (0,0,-1)
  Length = 35
  Length2 = 10
  Profile = -> Sketch163
  ReferenceAxis = -> Sketch163 [N_Axis]
  Type = 0
FEATURE [Sketcher::SketchObject] Sketch180
  ExternalGeometry = -> [Pad086]
  FullyConstrained = true
  MapMode = 5
  Placement = pos=(120,0,0) rot=(0.57735,0.57735,0.57735;2.0944rad)
  Support = -> [Pad086]
  sketch-geometry (17):
    g0: LineSegment StartX=6.85 StartY=-31 StartZ=0 EndX=23.85 EndY=-31 EndZ=0
    g1: LineSegment StartX=23.85 StartY=-31 StartZ=0 EndX=23.85 EndY=-16.5 EndZ=0
    g2: LineSegment StartX=23.85 StartY=-16.5 StartZ=0 EndX=6.85 EndY=-16.5 EndZ=0
    g3: LineSegment StartX=6.85 StartY=-16.5 StartZ=0 EndX=6.85 EndY=-31 EndZ=0
    g4: LineSegment StartX=26.1 StartY=-31 StartZ=0 EndX=42.1 EndY=-31 EndZ=0
    g5: LineSegment StartX=42.1 StartY=-31 StartZ=0 EndX=42.1 EndY=-14 EndZ=0
    g6: LineSegment StartX=42.1 StartY=-14 StartZ=0 EndX=26.1 EndY=-14 EndZ=0
    g7: LineSegment StartX=26.1 StartY=-14 StartZ=0 EndX=26.1 EndY=-31 EndZ=0
    g8: LineSegment StartX=44.1 StartY=-31 StartZ=0 EndX=60.1 EndY=-31 EndZ=0
    g9: LineSegment StartX=60.1 StartY=-31 StartZ=0 EndX=60.1 EndY=-14 EndZ=0
    g10: LineSegment StartX=60.1 StartY=-14 StartZ=0 EndX=44.1 EndY=-14 EndZ=0
    g11: LineSegment StartX=44.1 StartY=-14 StartZ=0 EndX=44.1 EndY=-31 EndZ=0
    g12: GeomPoint X=34.1 Y=-31 Z=0
    g13: GeomPoint X=52.1 Y=-31 Z=0
    g14: GeomPoint X=15.35 Y=-31 Z=0
    g15: GeomPoint X=8.6 Y=-30.5 Z=0
    g16: GeomPoint X=5.1 Y=-30.5 Z=0
  constraints (43):
    c: Coincident(g0,g1)
    c: Coincident(g1,g2)
    c: Coincident(g2,g3)
    c: Coincident(g3,g0)
    c: Horizontal(g0)
    c: Horizontal(g2)
    c: Vertical(g1)
    c: Vertical(g3)
    c: Coincident(g4,g5)
    c: Coincident(g5,g6)
    c: Coincident(g6,g7)
    c: Coincident(g7,g4)
    c: Horizontal(g4)
    c: Horizontal(g6)
    c: Vertical(g5)
    c: Vertical(g7)
    c: Coincident(g8,g9)
    c: Coincident(g9,g10)
    c: Coincident(g10,g11)
    c: Coincident(g11,g8)
    c: Horizontal(g8)
    c: Horizontal(g10)
    c: Vertical(g9)
    c: Vertical(g11)
    c: Horizontal(g0,g4)
    c: Horizontal(g4,g8)
    c: Horizontal(g10,g6)
    c: DistanceY(g9,g9) = 17
    c: Symmetric(g0,g0,g14)
    c: Symmetric(g4,g4,g12)
    c: Symmetric(g8,g8,g13)
    c: DistanceX(g15) = 8.6
    c: DistanceY(g-3,g15) = 4.5
    c: DistanceY(g14,g15) = 0.5
    c: Horizontal(g16,g15)
    c: DistanceX(g16,g15) = 3.5
    c: DistanceX(g16,g14) = 10.25
    c: DistanceX(g16,g12) = 29
    c: DistanceX(g16,g13) = 47
    c: Equal(g8,g4)
    c: DistanceX(g8,g8) = 16
    c: DistanceX(g2,g2) = 17
    c: DistanceY(g1,g1) = 14.5
FEATURE [PartDesign::Pocket] Pocket079
  BaseFeature = -> Pad086
  Direction = (-1,0,0)
  Length = 5
  Length2 = 5
  Profile = -> Sketch180
  ReferenceAxis = -> Sketch180 [N_Axis]
  Type = 0
FEATURE [Sketcher::SketchObject] Sketch181
  ExternalGeometry = -> [Pocket079]
  FullyConstrained = true
  MapMode = 5
  Placement = pos=(0,0,0) rot=(1,0,0;1.5708rad)
  Support = -> [Pocket079]
  sketch-geometry (17):
    g0: GeomPoint X=30.2 Y=-30.5 Z=0
    g1: LineSegment StartX=33.8 StartY=-33.15 StartZ=0 EndX=47.8 EndY=-33.15 EndZ=0
    g2: LineSegment StartX=47.8 StartY=-33.15 StartZ=0 EndX=47.8 EndY=-25.15 EndZ=0
    g3: LineSegment StartX=47.8 StartY=-25.15 StartZ=0 EndX=33.8 EndY=-25.15 EndZ=0
    g4: LineSegment StartX=33.8 StartY=-25.15 StartZ=0 EndX=33.8 EndY=-33.15 EndZ=0
    g5: LineSegment StartX=50.7 StartY=-35 StartZ=0 EndX=73.7 EndY=-35 EndZ=0
    g6: LineSegment StartX=73.7 StartY=-35 StartZ=0 EndX=73.7 EndY=-20 EndZ=0
    g7: LineSegment StartX=73.7 StartY=-20 StartZ=0 EndX=50.7 EndY=-20 EndZ=0
    g8: LineSegment StartX=50.7 StartY=-20 StartZ=0 EndX=50.7 EndY=-35 EndZ=0
    g9: LineSegment StartX=78.7 StartY=-22.5 StartZ=0 EndX=88.7 EndY=-22.5 EndZ=0
    g10: LineSegment StartX=88.7 StartY=-22.5 StartZ=0 EndX=88.7 EndY=-32.5 EndZ=0
    g11: LineSegment StartX=88.7 StartY=-32.5 StartZ=0 EndX=78.7 EndY=-32.5 EndZ=0
    g12: LineSegment StartX=78.7 StartY=-32.5 StartZ=0 EndX=78.7 EndY=-22.5 EndZ=0
    g13: GeomPoint X=40.8 Y=-33.15 Z=0
    g14: GeomPoint X=62.2 Y=-35 Z=0
    g15: GeomPoint X=83.7 Y=-32.5 Z=0
    g16: Circle CenterX=83 CenterY=-6.85 CenterZ=0 NormalX=0 NormalY=0 NormalZ=1 AngleXU=0 Radius=5.425
  constraints (44):
    c: DistanceY(g-3,g0) = 4.5
    c: DistanceX(g0,g-3) = 89.8
    c: Coincident(g1,g2)
    c: Coincident(g2,g3)
    c: Coincident(g3,g4)
    c: Coincident(g4,g1)
    c: Horizontal(g1)
    c: Horizontal(g3)
    c: Vertical(g2)
    c: Vertical(g4)
    c: Coincident(g5,g6)
    c: Coincident(g6,g7)
    c: Coincident(g7,g8)
    c: Coincident(g8,g5)
    c: Horizontal(g5)
    c: Horizontal(g7)
    c: Vertical(g6)
    c: Vertical(g8)
    c: Coincident(g9,g10)
    c: Coincident(g10,g11)
    c: Coincident(g11,g12)
    c: Coincident(g12,g9)
    c: Horizontal(g9)
    c: Horizontal(g11)
    c: Vertical(g10)
    c: Vertical(g12)
    c: DistanceX(g1,g1) = 14
    c: DistanceY(g2,g2) = 8
    c: Symmetric(g5,g5,g14)
    c: Symmetric(g11,g11,g15)
    c: Symmetric(g1,g1,g13)
    c: DistanceX(g0,g13) = 10.6
    c: DistanceY(g1,g0) = 2.65
    c: DistanceX(g0,g14) = 32
    c: DistanceX(g5,g5) = 23
    c: DistanceY(g6,g6) = 15
    c: PointOnObject(g5,g-3)
    c: DistanceX(g0,g15) = 53.5
    c: DistanceX(g11,g11) = 10
    c: DistanceY(g10,g10) = 10
    c: DistanceY(g11,g0) = 2
    c: Diameter(g16) = 10.85
    c: DistanceY(g16) = -6.85
    c: DistanceX(g16) = 83
FEATURE [PartDesign::Pocket] Pocket080
  BaseFeature = -> Pocket079
  Direction = (0,1,-2e-16)
  Length = 3
  Length2 = 5
  Profile = -> Sketch181
  ReferenceAxis = -> Sketch181 [N_Axis]
  Type = 0
FEATURE [Sketcher::SketchObject] Sketch185
  ExternalGeometry = -> [Pocket080]
  FullyConstrained = true
  MapMode = 5
  Placement = pos=(0,0,2.5) rot=(0,0,1;0rad)
  Support = -> [Pocket080]
  sketch-geometry (1):
    g0: Circle CenterX=113 CenterY=69.5 CenterZ=0 NormalX=0 NormalY=0 NormalZ=1 AngleXU=0 Radius=1.65
  constraints (3):
    c: Diameter(g0) = 3.3
    c: DistanceX(g0,g-3) = 7
    c: DistanceY(g0,g-3) = 3.5
FEATURE [PartDesign::Pocket] Pocket083
  BaseFeature = -> Pocket080
  Direction = (0,0,-1)
  Length = 5
  Length2 = 5
  Profile = -> Sketch185
  ReferenceAxis = -> Sketch185 [N_Axis]
  Type = 0
FEATURE [Sketcher::SketchObject] Sketch187
  FullyConstrained = true
  MapMode = 5
  Placement = pos=(0,0,-35) rot=(1,0,0;3.14159rad)
  Support = -> [Pocket083]
  sketch-geometry (6):
    g0: LineSegment StartX=0 StartY=0 StartZ=0 EndX=8 EndY=0 EndZ=0
    g1: LineSegment StartX=8 StartY=0 StartZ=0 EndX=8 EndY=5 EndZ=0
    g2: LineSegment StartX=8 StartY=5 StartZ=0 EndX=0 EndY=5 EndZ=0
    g3: LineSegment StartX=0 StartY=5 StartZ=0 EndX=0 EndY=0 EndZ=0
    g4: ArcOfCircle CenterX=4 CenterY=5 CenterZ=0 NormalX=0 NormalY=0 NormalZ=1 AngleXU=0 Radius=4 StartAngle=0 EndAngle=3.14159
    g5: Circle CenterX=4 CenterY=5 CenterZ=0 NormalX=0 NormalY=0 NormalZ=1 AngleXU=0 Radius=1.65
  constraints (16):
    c: Coincident(g0,g1)
    c: Coincident(g1,g2)
    c: Coincident(g2,g3)
    c: Coincident(g3,g0)
    c: Horizontal(g0)
    c: Horizontal(g2)
    c: Vertical(g1)
    c: Vertical(g3)
    c: Coincident(g0,g-1)
    c: PointOnObject(g4,g2)
    c: Coincident(g4,g2)
    c: Coincident(g4,g1)
    c: Diameter(g4) = 8
    c: DistanceY(g3,g3) = 5
    c: Coincident(g5,g4)
    c: Diameter(g5) = 3.3
FEATURE [PartDesign::Pad] Pad098
  BaseFeature = -> Pocket083
  Direction = (0,0,-1)
  Length = 4
  Length2 = 10
  Profile = -> Sketch187
  ReferenceAxis = -> Sketch187 [N_Axis]
  Reversed = true
  Type = 0
FEATURE [PartDesign::Fillet] Fillet071
  Base = -> Pad098 [Edge19]
  BaseFeature = -> Pad098
  Radius = 4
  SupportTransform = false
  UseAllEdges = false
FEATURE [PartDesign::Fillet] Fillet072
  Base = -> Fillet071 [Edge6,Edge4]
  BaseFeature = -> Fillet071
  Radius = 1.8
  SupportTransform = false
  UseAllEdges = false
FEATURE [Sketcher::SketchObject] Sketch189
  FullyConstrained = true
  MapMode = 5
  Placement = pos=(0,0,2.5) rot=(0,0,1;0rad)
  Support = -> [Fillet072]
  sketch-geometry (1):
    g0: Circle CenterX=25 CenterY=20 CenterZ=0 NormalX=0 NormalY=0 NormalZ=1 AngleXU=0 Radius=1
  constraints (3):
    c: Diameter(g0) = 2
    c: DistanceX(g0) = 25
    c: DistanceY(g0) = 20
FEATURE [PartDesign::Pocket] Pocket085
  BaseFeature = -> Fillet072
  Direction = (0,0,-1)
  Length = 2.5
  Length2 = 5
  Profile = -> Sketch189
  ReferenceAxis = -> Sketch189 [N_Axis]
  Type = 0
FEATURE [PartDesign::LinearPattern] LinearPattern
  Direction = -> Sketch189 [H_Axis]
  Length = 80
  Occurrences = 20
FEATURE [PartDesign::LinearPattern] LinearPattern001
  Direction = -> Sketch189 [V_Axis]
  Length = 40
  Occurrences = 10
FEATURE [PartDesign::MultiTransform] MultiTransform
  BaseFeature = -> Pocket085
  Originals = -> [Pocket085]
  Transformations = -> [LinearPattern,LinearPattern001]
FEATURE [Sketcher::SketchObject] Sketch190
  FullyConstrained = true
  MapMode = 5
  Placement = pos=(0,0,0) rot=(1,0,0;1.5708rad)
  Support = -> [MultiTransform]
  sketch-geometry (4):
    g0: ArcOfCircle CenterX=30 CenterY=-5.5 CenterZ=0 NormalX=0 NormalY=0 NormalZ=1 AngleXU=0 Radius=1 StartAngle=-2.363e-13 EndAngle=3.14159
    g1: ArcOfCircle CenterX=30 CenterY=-13.5 CenterZ=0 NormalX=0 NormalY=0 NormalZ=1 AngleXU=0 Radius=1 StartAngle=3.14159 EndAngle=6.28319
    g2: LineSegment StartX=29 StartY=-5.5 StartZ=0 EndX=29 EndY=-13.5 EndZ=0
    g3: LineSegment StartX=31 StartY=-13.5 StartZ=0 EndX=31 EndY=-5.5 EndZ=0
  constraints (10):
    c: Tangent(g0,g2) = -1.5708
    c: Tangent(g2,g1) = -1.5708
    c: Tangent(g1,g3) = -1.5708
    c: Tangent(g3,g0) = -1.5708
    c: Equal(g0,g1)
    c: Vertical(g2)
    c: Diameter(g0) = 2
    c: DistanceY(g3,g3) = 8
    c: DistanceX(g0) = 30
    c: DistanceY(g0) = -5.5
FEATURE [PartDesign::Pocket] Pocket086
  BaseFeature = -> MultiTransform
  Direction = (0,1,-2e-16)
  Length = 2.5
  Length2 = 5
  Profile = -> Sketch190
  ReferenceAxis = -> Sketch190 [N_Axis]
  Type = 0
FEATURE [PartDesign::LinearPattern] LinearPattern002
  BaseFeature = -> Pocket086
  Direction = -> Sketch190 [H_Axis]
  Length = 40
  Occurrences = 8
  Originals = -> [Pocket086]
FEATURE [PartDesign::Chamfer] Chamfer008
  Angle = 45
  Base = -> LinearPattern002 [Edge194,Edge185,Edge193,Edge64]
  BaseFeature = -> LinearPattern002
  ChamferType = 0
  FlipDirection = false
  Size = 1.75
  Size2 = 1
  SupportTransform = false
  UseAllEdges = false
FEATURE [PartDesign::Fillet] Fillet075
  Base = -> Chamfer008 [Edge73]
  BaseFeature = -> Chamfer008
  Radius = 3
  SupportTransform = false
  UseAllEdges = false
FEATURE [Sketcher::SketchObject] Sketch193
  FullyConstrained = true
  MapMode = 5
  Placement = pos=(0,2.5,0) rot=(0,0.707107,0.707107;3.14159rad)
  Support = -> [Fillet075]
  sketch-geometry (5):
    g0: LineSegment StartX=-75 StartY=0 StartZ=0 EndX=-91 EndY=0 EndZ=0
    g1: LineSegment StartX=-91 StartY=0 StartZ=0 EndX=-91 EndY=-8 EndZ=0
    g2: LineSegment StartX=-91 StartY=-8 StartZ=0 EndX=-75 EndY=-8 EndZ=0
    g3: LineSegment StartX=-75 StartY=-8 StartZ=0 EndX=-75 EndY=0 EndZ=0
    g4: ArcOfCircle CenterX=-83 CenterY=-8 CenterZ=0 NormalX=0 NormalY=0 NormalZ=1 AngleXU=0 Radius=8 StartAngle=3.14159 EndAngle=6.28319
  constraints (15):
    c: Coincident(g0,g1)
    c: Coincident(g1,g2)
    c: Coincident(g2,g3)
    c: Coincident(g3,g0)
    c: Horizontal(g0)
    c: Horizontal(g2)
    c: Vertical(g1)
    c: Vertical(g3)
    c: PointOnObject(g4,g2)
    c: Coincident(g4,g2)
    c: Coincident(g4,g1)
    c: DistanceY(g1,g1) = 8
    c: Diameter(g4) = 16
    c: DistanceX(g4) = -83
    c: PointOnObject(g0,g-1)
FEATURE [PartDesign::Pad] Pad099
  BaseFeature = -> Fillet075
  Direction = (0,1,-2e-16)
  Length = 3
  Length2 = 10
  Profile = -> Sketch193
  ReferenceAxis = -> Sketch193 [N_Axis]
  Type = 0
FEATURE [PartDesign::Fillet] Fillet076
  Base = -> Pad099 [Edge5,Edge1]
  BaseFeature = -> Pad099
  Radius = 3
  SupportTransform = false
  UseAllEdges = false
FEATURE [PartDesign::Fillet] Fillet077
  Base = -> Fillet076 [Edge649,Edge651,Edge648]
  BaseFeature = -> Fillet076
  Radius = 1
  SupportTransform = false
  UseAllEdges = false
FEATURE [PartDesign::Fillet] Fillet078
  Base = -> Fillet077 [Edge714,Edge237,Edge234,Edge226,Edge228,Edge222]
  BaseFeature = -> Fillet077
  Radius = 1
  SupportTransform = false
  UseAllEdges = false
FEATURE [PartDesign::Fillet] Fillet087
  Base = -> Fillet078 [Face232,Face233,Face237,Face236,Face241,Face240,Face239,Face238,Face235,Face234,Face231,Face230]
  BaseFeature = -> Fillet078
  Radius = 0.8
  SupportTransform = false
  UseAllEdges = false
FEATURE [PartDesign::Fillet] Fillet088
  Base = -> Fillet087 [Face300,Face299,Face298,Face297,Face292,Face291,Face46,Face293,Face296,Face294,Face295]
  BaseFeature = -> Fillet087
  Radius = 1
  SupportTransform = false
  UseAllEdges = false
FEATURE [PartDesign::Fillet] Fillet089
  Base = -> Fillet088 [Face55,Face52,Face53,Face49,Face48,Face51,Face47,Face44,Face45,Face41,Face40,Face43,Face39,Face36,Face37,Face33,Face32,Face35,Face31,Face28,Face27,Face24,Face25,Face29,Face54,Face50,Face46,Face42,Face38,Face34,Face30,Face26]
  BaseFeature = -> Fillet088
  Radius = 1
  SupportTransform = false
  UseAllEdges = false
FEATURE [PartDesign::Fillet] Fillet090
  Base = -> Fillet089 [Face251,Face254,Face263,Face284,Face287,Face296,Face371,Face374,Face383,Face404,Face405,Face384,Face375,Face372,Face297,Face288,Face285,Face264,Face255,Face252,Face253,Face257,Face260,Face256,Face265,Face266,Face290,Face286,Face289,Face293,Face299,Face298,Face373,Face377,Face380,Face376,Face385,Face406,Face407,Face386,+160 more]
  BaseFeature = -> Fillet089
  Radius = 1
  SupportTransform = false
  UseAllEdges = false
FEATURE [Sketcher::SketchObject] Sketch195
  ExternalGeometry = -> [Fillet090]
  FullyConstrained = true
  MapMode = 5
  Placement = pos=(0,2.5,-5e-16) rot=(1,0,0;1.5708rad)
  Support = -> [Fillet090]
  sketch-geometry (2):
    g0: GeomPoint X=83 Y=-1.425 Z=0
    g1: Circle CenterX=83 CenterY=-6.85 CenterZ=0 NormalX=0 NormalY=0 NormalZ=1 AngleXU=0 Radius=5.425
  constraints (4):
    c: PointOnObject(g0,g-3)
    c: Vertical(g0,g-3)
    c: Coincident(g1,g-3)
    c: PointOnObject(g0,g1)
FEATURE [PartDesign::Pocket] Pocket089
  BaseFeature = -> Fillet090
  Direction = (0,1,-2e-16)
  Length = 5
  Length2 = 5
  Profile = -> Sketch195
  ReferenceAxis = -> Sketch195 [N_Axis]
  Type = 0
FEATURE [PartDesign::Body] Body032
  Group = -> [Sketch161,Pad084,Sketch163,Pad086,Sketch180,Pocket079,Sketch181,Pocket080,Sketch185,Pocket083,Sketch187,Pad098,Fillet071,Fillet072,Sketch189,Pocket085,MultiTransform,LinearPattern,LinearPattern001,Sketch190,Pocket086,LinearPattern002,Chamfer008,Fillet075,Sketch193,Pad099,Fillet076,Fillet077,Fillet078,Fillet087,Fillet088,Fillet089,Fillet090,Sketch195,Pocket089]
  Origin = -> Origin031
  Tip = -> Pocket089
COMPONENT P36 — recipe-attached ("Body033", modeled in this document).
Construction recipe (the document's own serialized feature program — sketch geometry with constraints, then the solid features built on it; lengths are millimeters unless a unit is written):

FEATURE [Sketcher::SketchObject] Sketch160
  FullyConstrained = true
  MapMode = 5
  Support = -> [XY_Plane032]
  sketch-geometry (4):
    g0: LineSegment StartX=0 StartY=0 StartZ=0 EndX=120 EndY=0 EndZ=0
    g1: LineSegment StartX=120 StartY=0 StartZ=0 EndX=120 EndY=73 EndZ=0
    g2: LineSegment StartX=120 StartY=73 StartZ=0 EndX=0 EndY=73 EndZ=0
    g3: LineSegment StartX=0 StartY=73 StartZ=0 EndX=0 EndY=0 EndZ=0
  constraints (11):
    c: Coincident(g0,g1)
    c: Coincident(g1,g2)
    c: Coincident(g2,g3)
    c: Coincident(g3,g0)
    c: Horizontal(g0)
    c: Horizontal(g2)
    c: Vertical(g1)
    c: Vertical(g3)
    c: Coincident(g0,g-1)
    c: DistanceY(g1,g1) = 73
    c: DistanceX(g0,g0) = 120
FEATURE [PartDesign::Pad] Pad083
  Direction = (0,0,1)
  Length = 2.5
  Length2 = 10
  Profile = -> Sketch160
  ReferenceAxis = -> Sketch160 [N_Axis]
  Type = 0
FEATURE [Sketcher::SketchObject] Sketch162
  ExternalGeometry = -> [Pad083]
  FullyConstrained = true
  MapMode = 5
  Placement = pos=(0,0,2.5) rot=(0,0,1;0rad)
  Support = -> [Pad083]
  sketch-geometry (14):
    g0: LineSegment StartX=0 StartY=73 StartZ=0 EndX=120 EndY=73 EndZ=0
    g1: LineSegment StartX=0 StartY=70.5 StartZ=0 EndX=0 EndY=73 EndZ=0
    g2: LineSegment StartX=22 StartY=70.5 StartZ=0 EndX=22 EndY=63.5 EndZ=0
    g3: LineSegment StartX=22 StartY=63.5 StartZ=0 EndX=15 EndY=63.5 EndZ=0
    g4: LineSegment StartX=15 StartY=63.5 StartZ=0 EndX=15 EndY=70.5 EndZ=0
    g5: LineSegment StartX=15 StartY=70.5 StartZ=0 EndX=0 EndY=70.5 EndZ=0
    g6: LineSegment StartX=15 StartY=11.5 StartZ=0 EndX=22 EndY=11.5 EndZ=0
    g7: LineSegment StartX=22 StartY=11.5 StartZ=0 EndX=22 EndY=4 EndZ=0
    g8: LineSegment StartX=22 StartY=4 StartZ=0 EndX=15 EndY=4 EndZ=0
    g9: LineSegment StartX=15 StartY=4 StartZ=0 EndX=15 EndY=11.5 EndZ=0
    g10: LineSegment StartX=22 StartY=70.5 StartZ=0 EndX=104.5 EndY=70.5 EndZ=0
    g11: LineSegment StartX=104.5 StartY=70.5 StartZ=0 EndX=110 EndY=65 EndZ=0
    g12: LineSegment StartX=110 StartY=65 StartZ=0 EndX=120 EndY=65 EndZ=0
    g13: LineSegment StartX=120 StartY=65 StartZ=0 EndX=120 EndY=73 EndZ=0
  constraints (40):
    c: Coincident(g0,g-6)
    c: Coincident(g0,g-6)
    c: PointOnObject(g5,g-3)
    c: Coincident(g1,g5)
    c: Coincident(g1,g0)
    c: Coincident(g2,g3)
    c: Coincident(g3,g4)
    c: Horizontal(g3)
    c: Vertical(g2)
    c: Vertical(g4)
    c: DistanceX(g4) = 15
    c: DistanceX(g3,g3) = 7
    c: DistanceY(g2,g2) = 7
    c: Coincident(g4,g5)
    c: Horizontal(g5)
    c: Horizontal(g4,g2)
    c: Coincident(g6,g7)
    c: Coincident(g7,g8)
    c: Coincident(g8,g9)
    c: Coincident(g9,g6)
    c: Horizontal(g6)
    c: Horizontal(g8)
    c: Vertical(g7)
    c: Vertical(g9)
    c: Vertical(g6,g3)
    c: Vertical(g6,g2)
    c: DistanceY(g8) = 4
    c: DistanceY(g9,g9) = 7.5
    c: Coincident(g10,g2)
    c: Horizontal(g10)
    c: Coincident(g11,g10)
    c: Coincident(g12,g11)
    c: PointOnObject(g12,g-5)
    c: Horizontal(g12)
    c: Coincident(g13,g12)
    c: Coincident(g13,g0)
    c: DistanceX(g12,g12) = 10
    c: DistanceY(g13,g13) = 8
    c: DistanceY(g10,g0) = 2.5
    c: Angle(g10,g11) = 2.35619
FEATURE [PartDesign::Pad] Pad085
  BaseFeature = -> Pad083
  Direction = (0,0,1)
  Length = 35
  Length2 = 10
  Profile = -> Sketch162
  ReferenceAxis = -> Sketch162 [N_Axis]
  Type = 0
FEATURE [Sketcher::SketchObject] Sketch169
  ExternalGeometry = -> [Pad085]
  FullyConstrained = true
  MapMode = 5
  Placement = pos=(120,-2.136e-13,0) rot=(0.57735,0.57735,0.57735;2.0944rad)
  Support = -> [Pad085]
  sketch-geometry (4):
    g0: LineSegment StartX=65 StartY=0 StartZ=0 EndX=73 EndY=0 EndZ=0
    g1: LineSegment StartX=73 StartY=0 StartZ=0 EndX=73 EndY=37.5 EndZ=0
    g2: LineSegment StartX=73 StartY=37.5 StartZ=0 EndX=65 EndY=37.5 EndZ=0
    g3: LineSegment StartX=65 StartY=37.5 StartZ=0 EndX=65 EndY=0 EndZ=0
  constraints (11):
    c: Coincident(g0,g1)
    c: Coincident(g1,g2)
    c: Coincident(g2,g3)
    c: Coincident(g3,g0)
    c: Horizontal(g0)
    c: Horizontal(g2)
    c: Vertical(g1)
    c: Vertical(g3)
    c: PointOnObject(g0,g-1)
    c: Coincident(g1,g-3)
    c: DistanceX(g0,g0) = 8
FEATURE [PartDesign::Pad] Pad091
  BaseFeature = -> Pad085
  Direction = (1,-1.8e-15,0)
  Length = 14
  Length2 = 10
  Profile = -> Sketch169
  ReferenceAxis = -> Sketch169 [N_Axis]
  Type = 0
FEATURE [Sketcher::SketchObject] Sketch170
  ExternalGeometry = -> [Pad091]
  FullyConstrained = true
  MapMode = 5
  Placement = pos=(1.157e-13,65,0) rot=(1,0,0;1.5708rad)
  Support = -> [Pad091]
  sketch-geometry (4):
    g0: ArcOfCircle CenterX=126 CenterY=29.5 CenterZ=0 NormalX=0 NormalY=0 NormalZ=1 AngleXU=0 Radius=6 StartAngle=-9e-16 EndAngle=3.14159
    g1: ArcOfCircle CenterX=126 CenterY=8 CenterZ=0 NormalX=0 NormalY=0 NormalZ=1 AngleXU=0 Radius=6 StartAngle=3.14159 EndAngle=6.28319
    g2: LineSegment StartX=120 StartY=29.5 StartZ=0 EndX=120 EndY=8 EndZ=0
    g3: LineSegment StartX=132 StartY=8 StartZ=0 EndX=132 EndY=29.5 EndZ=0
  constraints (10):
    c: Tangent(g0,g2) = -1.5708
    c: Tangent(g2,g1) = -1.5708
    c: Tangent(g1,g3) = -1.5708
    c: Tangent(g3,g0) = -1.5708
    c: Equal(g0,g1)
    c: Vertical(g2)
    c: Diameter(g1) = 12
    c: PointOnObject(g0,g-3)
    c: DistanceY(g0,g-3) = 8
    c: DistanceY(g1) = 8
FEATURE [PartDesign::Pocket] Pocket073
  BaseFeature = -> Pad091
  Direction = (1.8e-15,1,-2e-16)
  Length = 5
  Length2 = 5
  Profile = -> Sketch170
  ReferenceAxis = -> Sketch170 [N_Axis]
  Type = 0
FEATURE [Sketcher::SketchObject] Sketch171
  ExternalGeometry = -> [Pocket073]
  FullyConstrained = true
  MapMode = 5
  Placement = pos=(9.1e-14,70,0) rot=(1,0,0;1.5708rad)
  Support = -> [Pocket073]
  sketch-geometry (4):
    g0: Circle CenterX=126 CenterY=29.5 CenterZ=0 NormalX=0 NormalY=0 NormalZ=1 AngleXU=0 Radius=3.15
    g1: Circle CenterX=126 CenterY=18.75 CenterZ=0 NormalX=0 NormalY=0 NormalZ=1 AngleXU=0 Radius=3.15
    g2: Circle CenterX=126 CenterY=8 CenterZ=0 NormalX=0 NormalY=0 NormalZ=1 AngleXU=0 Radius=3.15
    g3: LineSegment StartX=126 StartY=8 StartZ=0 EndX=126 EndY=29.5 EndZ=0
  constraints (8):
    c: Coincident(g0,g-4)
    c: Coincident(g2,g-3)
    c: Equal(g2,g1)
    c: Equal(g1,g0)
    c: Coincident(g3,g2)
    c: Coincident(g3,g0)
    c: Symmetric(g3,g3,g1)
    c: Diameter(g1) = 6.3
FEATURE [PartDesign::Pocket] Pocket074
  BaseFeature = -> Pocket073
  Direction = (1.3e-15,1,-2e-16)
  Length = 5
  Length2 = 5
  Profile = -> Sketch171
  ReferenceAxis = -> Sketch171 [N_Axis]
  Type = 0
FEATURE [Sketcher::SketchObject] Sketch172
  ExternalGeometry = -> [Pocket074]
  FullyConstrained = true
  MapMode = 5
  Placement = pos=(0,0,2.5) rot=(0,0,1;0rad)
  Support = -> [Pocket074]
  sketch-geometry (4):
    g0: Circle CenterX=33.7 CenterY=57.6 CenterZ=0 NormalX=0 NormalY=0 NormalZ=1 AngleXU=0 Radius=3
    g1: Circle CenterX=91.7 CenterY=57.6 CenterZ=0 NormalX=0 NormalY=0 NormalZ=1 AngleXU=0 Radius=3
    g2: Circle CenterX=91.7 CenterY=8.6 CenterZ=0 NormalX=0 NormalY=0 NormalZ=1 AngleXU=0 Radius=3
    g3: Circle CenterX=33.7 CenterY=8.6 CenterZ=0 NormalX=0 NormalY=0 NormalZ=1 AngleXU=0 Radius=3
  constraints (12):
    c: Equal(g0,g1)
    c: Equal(g1,g2)
    c: Equal(g2,g3)
    c: Diameter(g2) = 6
    c: DistanceX(g2,g-3) = 28.3
    c: DistanceX(g3,g2) = 58
    c: Horizontal(g3,g2)
    c: Vertical(g1,g2)
    c: Horizontal(g1,g0)
    c: DistanceY(g2,g1) = 49
    c: Vertical(g0,g3)
    c: DistanceY(g2) = 8.6
FEATURE [PartDesign::Pad] Pad092
  BaseFeature = -> Pocket074
  Direction = (0,0,1)
  Length = 3
  Length2 = 10
  Profile = -> Sketch172
  ReferenceAxis = -> Sketch172 [N_Axis]
  Type = 0
FEATURE [Sketcher::SketchObject] Sketch173
  ExternalGeometry = -> [Pad092]
  FullyConstrained = true
  MapMode = 5
  Placement = pos=(0,0,5.5) rot=(0,0,1;0rad)
  Support = -> [Pad092]
  sketch-geometry (4):
    g0: Circle CenterX=33.7 CenterY=57.6 CenterZ=0 NormalX=0 NormalY=0 NormalZ=1 AngleXU=0 Radius=1.45
    g1: Circle CenterX=91.7 CenterY=57.6 CenterZ=0 NormalX=0 NormalY=0 NormalZ=1 AngleXU=0 Radius=1.45
    g2: Circle CenterX=91.7 CenterY=8.6 CenterZ=0 NormalX=0 NormalY=0 NormalZ=1 AngleXU=0 Radius=1.45
    g3: Circle CenterX=33.7 CenterY=8.6 CenterZ=0 NormalX=0 NormalY=0 NormalZ=1 AngleXU=0 Radius=1.45
  constraints (8):
    c: Coincident(g0,g-3)
    c: Coincident(g1,g-4)
    c: Coincident(g2,g-5)
    c: Coincident(g3,g-6)
    c: Equal(g0,g1)
    c: Equal(g1,g2)
    c: Equal(g2,g3)
    c: Diameter(g1) = 2.9
FEATURE [PartDesign::Pocket] Pocket075
  BaseFeature = -> Pad092
  Direction = (0,0,-1)
  Length = 5
  Length2 = 5
  Profile = -> Sketch173
  ReferenceAxis = -> Sketch173 [N_Axis]
  Type = 1
FEATURE [Sketcher::SketchObject] Sketch174
  FullyConstrained = true
  MapMode = 5
  Placement = pos=(15,0,0) rot=(0.57735,-0.57735,-0.57735;2.0944rad)
  Support = -> [Pocket075]
  sketch-geometry (4):
    g0: Circle CenterX=-66.6 CenterY=30 CenterZ=0 NormalX=0 NormalY=0 NormalZ=1 AngleXU=0 Radius=1.65
    g1: Circle CenterX=-66.6 CenterY=7 CenterZ=0 NormalX=0 NormalY=0 NormalZ=1 AngleXU=0 Radius=1.65
    g2: Circle CenterX=-8.6 CenterY=30 CenterZ=0 NormalX=0 NormalY=0 NormalZ=1 AngleXU=0 Radius=1.65
    g3: Circle CenterX=-8.6 CenterY=7 CenterZ=0 NormalX=0 NormalY=0 NormalZ=1 AngleXU=0 Radius=1.65
  constraints (12):
    c: Vertical(g2,g3)
    c: Horizontal(g0,g2)
    c: Horizontal(g1,g3)
    c: Vertical(g1,g0)
    c: Equal(g0,g1)
    c: Equal(g1,g2)
    c: Equal(g2,g3)
    c: Diameter(g2) = 3.3
    c: DistanceX(g3) = -8.6
    c: DistanceX(g1,g3) = 58
    c: DistanceY(g3,g2) = 23
    c: DistanceY(g3) = 7
FEATURE [PartDesign::Pocket] Pocket076
  BaseFeature = -> Pocket075
  Direction = (1,0,0)
  Length = 10
  Length2 = 5
  Profile = -> Sketch174
  ReferenceAxis = -> Sketch174 [N_Axis]
  Type = 0
FEATURE [Sketcher::SketchObject] Sketch175
  ExternalGeometry = -> [Pocket076]
  FullyConstrained = true
  MapMode = 5
  Placement = pos=(22,0,0) rot=(0.57735,0.57735,0.57735;2.0944rad)
  Support = -> [Pocket076]
  sketch-geometry (28):
    g0: LineSegment StartX=11.35 StartY=31.5877 StartZ=0 EndX=8.6 EndY=33.1754 EndZ=0
    g1: LineSegment StartX=8.6 StartY=33.1754 StartZ=0 EndX=5.85 EndY=31.5877 EndZ=0
    g2: LineSegment StartX=5.85 StartY=31.5877 StartZ=0 EndX=5.85 EndY=28.4123 EndZ=0
    g3: LineSegment StartX=5.85 StartY=28.4123 StartZ=0 EndX=8.6 EndY=26.8246 EndZ=0
    g4: LineSegment StartX=8.6 StartY=26.8246 StartZ=0 EndX=11.35 EndY=28.4123 EndZ=0
    g5: LineSegment StartX=11.35 StartY=28.4123 StartZ=0 EndX=11.35 EndY=31.5877 EndZ=0
    g6: Circle CenterX=8.6 CenterY=30 CenterZ=0 NormalX=0 NormalY=0 NormalZ=1 AngleXU=0 Radius=3.17543
    g7: LineSegment StartX=11.35 StartY=8.58771 StartZ=0 EndX=8.6 EndY=10.1754 EndZ=0
    g8: LineSegment StartX=8.6 StartY=10.1754 StartZ=0 EndX=5.85 EndY=8.58771 EndZ=0
    g9: LineSegment StartX=5.85 StartY=8.58771 StartZ=0 EndX=5.85 EndY=5.41229 EndZ=0
    g10: LineSegment StartX=5.85 StartY=5.41229 StartZ=0 EndX=8.6 EndY=3.82457 EndZ=0
    g11: LineSegment StartX=8.6 StartY=3.82457 StartZ=0 EndX=11.35 EndY=5.41229 EndZ=0
    g12: LineSegment StartX=11.35 StartY=5.41229 StartZ=0 EndX=11.35 EndY=8.58771 EndZ=0
    g13: Circle CenterX=8.6 CenterY=7 CenterZ=0 NormalX=0 NormalY=0 NormalZ=1 AngleXU=0 Radius=3.17543
    g14: LineSegment StartX=69.35 StartY=31.5877 StartZ=0 EndX=66.6 EndY=33.1754 EndZ=0
    g15: LineSegment StartX=66.6 StartY=33.1754 StartZ=0 EndX=63.85 EndY=31.5877 EndZ=0
    g16: LineSegment StartX=63.85 StartY=31.5877 StartZ=0 EndX=63.85 EndY=28.4123 EndZ=0
    g17: LineSegment StartX=63.85 StartY=28.4123 StartZ=0 EndX=66.6 EndY=26.8246 EndZ=0
    g18: LineSegment StartX=66.6 StartY=26.8246 StartZ=0 EndX=69.35 EndY=28.4123 EndZ=0
    g19: LineSegment StartX=69.35 StartY=28.4123 StartZ=0 EndX=69.35 EndY=31.5877 EndZ=0
    g20: Circle CenterX=66.6 CenterY=30 CenterZ=0 NormalX=0 NormalY=0 NormalZ=1 AngleXU=0 Radius=3.17543
    g21: LineSegment StartX=69.35 StartY=8.58771 StartZ=0 EndX=66.6 EndY=10.1754 EndZ=0
    g22: LineSegment StartX=66.6 StartY=10.1754 StartZ=0 EndX=63.85 EndY=8.58771 EndZ=0
    g23: LineSegment StartX=63.85 StartY=8.58771 StartZ=0 EndX=63.85 EndY=5.41229 EndZ=0
    g24: LineSegment StartX=63.85 StartY=5.41229 StartZ=0 EndX=66.6 EndY=3.82457 EndZ=0
    g25: LineSegment StartX=66.6 StartY=3.82457 StartZ=0 EndX=69.35 EndY=5.41229 EndZ=0
    g26: LineSegment StartX=69.35 StartY=5.41229 StartZ=0 EndX=69.35 EndY=8.58771 EndZ=0
    g27: Circle CenterX=66.6 CenterY=7 CenterZ=0 NormalX=0 NormalY=0 NormalZ=1 AngleXU=0 Radius=3.17543
  constraints (64):
    c: Coincident(g0,g1)
    c: Coincident(g1,g2)
    c: Coincident(g2,g3)
    c: Coincident(g3,g4)
    c: Coincident(g4,g5)
    c: Coincident(g5,g0)
    c: Equal(g0, g1-g5) x5
    c: PointOnObject(g0,g6)
    c: PointOnObject(g1,g6)
    c: PointOnObject(g2,g6)
    c: PointOnObject(g3,g6)
    c: PointOnObject(g4,g6)
    c: PointOnObject(g5,g6)
    c: Coincident(g6,g-3)
    c: Coincident(g7,g8)
    c: Coincident(g8,g9)
    c: Coincident(g9,g10)
    c: Coincident(g10,g11)
    c: Coincident(g11,g12)
    c: Coincident(g12,g7)
    c: Equal(g7, g8-g12) x5
    c: PointOnObject(g7,g13)
    c: PointOnObject(g8,g13)
    c: PointOnObject(g9,g13)
    c: PointOnObject(g10,g13)
    c: PointOnObject(g11,g13)
    c: PointOnObject(g12,g13)
    c: Coincident(g13,g-6)
    c: Coincident(g14,g15)
    c: Coincident(g15,g16)
    c: Coincident(g16,g17)
    c: Coincident(g17,g18)
    c: Coincident(g18,g19)
    c: Coincident(g19,g14)
    c: Equal(g14, g15-g19) x5
    c: PointOnObject(g14,g20)
    c: PointOnObject(g15,g20)
    c: PointOnObject(g16,g20)
    c: PointOnObject(g17,g20)
    c: PointOnObject(g18,g20)
    c: PointOnObject(g19,g20)
    c: Coincident(g20,g-4)
    c: Coincident(g21,g22)
    c: Coincident(g22,g23)
    c: Coincident(g23,g24)
    c: Coincident(g24,g25)
    c: Coincident(g25,g26)
    c: Coincident(g26,g21)
    c: Equal(g21, g22-g26) x5
    c: PointOnObject(g21,g27)
    c: PointOnObject(g22,g27)
    c: PointOnObject(g23,g27)
    c: PointOnObject(g24,g27)
    c: PointOnObject(g25,g27)
    c: PointOnObject(g26,g27)
    c: Coincident(g27,g-5)
    c: Vertical(g12)
    c: Vertical(g5)
    c: Vertical(g19)
    c: Vertical(g26)
    c: Equal(g27,g20)
    c: Equal(g20,g6)
    c: Equal(g6,g13)
    c: Distance(g7,g9) = 5.5
FEATURE [PartDesign::Pocket] Pocket077
  BaseFeature = -> Pocket076
  Direction = (-1,0,0)
  Length = 2.75
  Length2 = 5
  Profile = -> Sketch175
  ReferenceAxis = -> Sketch175 [N_Axis]
  Type = 0
FEATURE [Sketcher::SketchObject] Sketch176
  ExternalGeometry = -> [Pocket077]
  FullyConstrained = true
  MapMode = 5
  Placement = pos=(22,0,0) rot=(0.57735,0.57735,0.57735;2.0944rad)
  Support = -> [Pocket077]
  sketch-geometry (8):
    g0: LineSegment StartX=11.5 StartY=14.5 StartZ=0 EndX=13.1 EndY=12.0751 EndZ=0
    g1: LineSegment StartX=13.1 StartY=12.0751 StartZ=0 EndX=13.1 EndY=2.5 EndZ=0
    g2: LineSegment StartX=11.5 StartY=2.5 StartZ=0 EndX=13.1 EndY=2.5 EndZ=0
    g3: LineSegment StartX=11.5 StartY=2.5 StartZ=0 EndX=11.5 EndY=14.5 EndZ=0
    g4: LineSegment StartX=63.5 StartY=2.5 StartZ=0 EndX=63.5 EndY=14.5 EndZ=0
    g5: LineSegment StartX=63.5 StartY=14.5 StartZ=0 EndX=62.1 EndY=12.0751 EndZ=0
    g6: LineSegment StartX=62.1 StartY=12.0751 StartZ=0 EndX=62.1 EndY=2.5 EndZ=0
    g7: LineSegment StartX=62.1 StartY=2.5 StartZ=0 EndX=63.5 EndY=2.5 EndZ=0
  constraints (22):
    c: PointOnObject(g0,g-6)
    c: Coincident(g1,g0)
    c: Vertical(g1)
    c: Coincident(g2,g-6)
    c: Horizontal(g2)
    c: Coincident(g3,g2)
    c: Coincident(g3,g0)
    c: Coincident(g1,g2)
    c: DistanceX(g-3,g1) = 4.5
    c: Coincident(g4,g-5)
    c: PointOnObject(g4,g-5)
    c: Coincident(g5,g4)
    c: Coincident(g6,g5)
    c: Vertical(g6)
    c: Coincident(g7,g6)
    c: Coincident(g7,g4)
    c: Horizontal(g7)
    c: Horizontal(g5,g0)
    c: Horizontal(g0,g4)
    c: DistanceX(g6,g-4) = 4.5
    c: Angle(g5,g4) = 0.523599
    c: DistanceY(g4,g4) = 12
FEATURE [PartDesign::Pad] Pad093
  BaseFeature = -> Pocket077
  Direction = (1,0,0)
  Length = 7
  Length2 = 10
  Profile = -> Sketch176
  ReferenceAxis = -> Sketch176 [N_Axis]
  Reversed = true
  Type = 0
FEATURE [Sketcher::SketchObject] Sketch182
  ExternalGeometry = -> [Pad093]
  FullyConstrained = true
  MapMode = 5
  Placement = pos=(0,0,37.5) rot=(0,0,1;0rad)
  Support = -> [Pad093]
  sketch-geometry (10):
    g0: LineSegment StartX=115.75 StartY=71.0877 StartZ=0 EndX=113 EndY=72.6754 EndZ=0
    g1: LineSegment StartX=113 StartY=72.6754 StartZ=0 EndX=110.25 EndY=71.0877 EndZ=0
    g2: LineSegment StartX=110.25 StartY=71.0877 StartZ=0 EndX=110.25 EndY=67.9123 EndZ=0
    g3: LineSegment StartX=110.25 StartY=67.9123 StartZ=0 EndX=113 EndY=66.3246 EndZ=0
    g4: LineSegment StartX=113 StartY=66.3246 StartZ=0 EndX=115.75 EndY=67.9123 EndZ=0
    g5: LineSegment StartX=115.75 StartY=67.9123 StartZ=0 EndX=115.75 EndY=71.0877 EndZ=0
    g6: Circle CenterX=113 CenterY=69.5 CenterZ=0 NormalX=0 NormalY=0 NormalZ=1 AngleXU=0 Radius=3.17543
    g7: LineSegment StartX=110.25 StartY=71.0877 StartZ=0 EndX=110.25 EndY=73 EndZ=0
    g8: LineSegment StartX=115.75 StartY=71.0877 StartZ=0 EndX=115.75 EndY=73 EndZ=0
    g9: LineSegment StartX=115.75 StartY=73 StartZ=0 EndX=110.25 EndY=73 EndZ=0
  constraints (25):
    c: Coincident(g0,g1)
    c: Coincident(g1,g2)
    c: Coincident(g2,g3)
    c: Coincident(g3,g4)
    c: Coincident(g4,g5)
    c: Coincident(g5,g0)
    c: Equal(g0, g1-g5) x5
    c: PointOnObject(g0,g6)
    c: PointOnObject(g1,g6)
    c: PointOnObject(g2,g6)
    c: PointOnObject(g3,g6)
    c: PointOnObject(g4,g6)
    c: PointOnObject(g5,g6)
    c: Vertical(g5)
    c: Coincident(g7,g2)
    c: PointOnObject(g7,g-3)
    c: Vertical(g7)
    c: Coincident(g8,g5)
    c: PointOnObject(g8,g-3)
    c: Vertical(g8)
    c: Coincident(g9,g8)
    c: Coincident(g9,g7)
    c: DistanceX(g9,g9) = 5.5
    c: DistanceX(g0,g-3) = 7
    c: DistanceY(g6,g-3) = 3.5
FEATURE [PartDesign::Pocket] Pocket081
  BaseFeature = -> Pad093
  Direction = (0,0,-1)
  Length = 10
  Length2 = 5
  Profile = -> Sketch182
  ReferenceAxis = -> Sketch182 [N_Axis]
  Type = 0
FEATURE [Sketcher::SketchObject] Sketch183
  ExternalGeometry = -> [Pocket081]
  FullyConstrained = true
  MapMode = 5
  Placement = pos=(0,0,37.5) rot=(0,0,1;0rad)
  Support = -> [Pocket081]
  sketch-geometry (5):
    g0: LineSegment StartX=110.25 StartY=73 StartZ=0 EndX=115.75 EndY=73 EndZ=0
    g1: LineSegment StartX=110.25 StartY=73 StartZ=0 EndX=110.25 EndY=67.9123 EndZ=0
    g2: LineSegment StartX=110.25 StartY=67.9123 StartZ=0 EndX=113 EndY=66.3246 EndZ=0
    g3: LineSegment StartX=113 StartY=66.3246 StartZ=0 EndX=115.75 EndY=67.9123 EndZ=0
    g4: LineSegment StartX=115.75 StartY=67.9123 StartZ=0 EndX=115.75 EndY=73 EndZ=0
  constraints (10):
    c: Coincident(g0,g-4)
    c: Coincident(g0,g-3)
    c: Coincident(g1,g0)
    c: Coincident(g1,g-6)
    c: Coincident(g2,g1)
    c: Coincident(g2,g-7)
    c: Coincident(g3,g2)
    c: Coincident(g3,g-7)
    c: Coincident(g4,g3)
    c: Coincident(g4,g0)
FEATURE [PartDesign::Pad] Pad096
  BaseFeature = -> Pocket081
  Direction = (0,0,1)
  Length = 5
  Length2 = 10
  Profile = -> Sketch183
  ReferenceAxis = -> Sketch183 [N_Axis]
  Reversed = true
  Type = 0
FEATURE [Sketcher::SketchObject] Sketch184
  ExternalGeometry = -> [Pad096]
  FullyConstrained = true
  MapMode = 5
  Placement = pos=(0,0,37.5) rot=(0,0,1;0rad)
  Support = -> [Pad096]
  sketch-geometry (3):
    g0: LineSegment StartX=110.25 StartY=67.9123 StartZ=0 EndX=113 EndY=69.5 EndZ=0
    g1: LineSegment StartX=113 StartY=69.5 StartZ=0 EndX=113 EndY=66.3246 EndZ=0
    g2: Circle CenterX=113 CenterY=69.5 CenterZ=0 NormalX=0 NormalY=0 NormalZ=1 AngleXU=0 Radius=1.65
  constraints (7):
    c: Coincident(g0,g-3)
    c: Coincident(g1,g0)
    c: Coincident(g1,g-4)
    c: Vertical(g1)
    c: Equal(g0,g1)
    c: Coincident(g2,g0)
    c: Diameter(g2) = 3.3
FEATURE [PartDesign::Pocket] Pocket082
  BaseFeature = -> Pad096
  Direction = (0,0,-1)
  Length = 5
  Length2 = 5
  Profile = -> Sketch184
  ReferenceAxis = -> Sketch184 [N_Axis]
  Type = 1
FEATURE [PartDesign::Fillet] Fillet069
  Base = -> Pocket082 [Edge161,Edge52]
  BaseFeature = -> Pocket082
  Radius = 8
  SupportTransform = false
  UseAllEdges = false
FEATURE [Sketcher::SketchObject] Sketch186
  FullyConstrained = true
  MapMode = 5
  Placement = pos=(0,0,0) rot=(1,0,0;3.14159rad)
  Support = -> [Fillet069]
  sketch-geometry (5):
    g0: LineSegment StartX=0 StartY=0 StartZ=0 EndX=0 EndY=5 EndZ=0
    g1: LineSegment StartX=8 StartY=0 StartZ=0 EndX=8 EndY=5 EndZ=0
    g2: ArcOfCircle CenterX=4 CenterY=5 CenterZ=0 NormalX=0 NormalY=0 NormalZ=1 AngleXU=0 Radius=4 StartAngle=0 EndAngle=3.14159
    g3: LineSegment StartX=0 StartY=0 StartZ=0 EndX=8 EndY=0 EndZ=0
    g4: Circle CenterX=4 CenterY=5 CenterZ=0 NormalX=0 NormalY=0 NormalZ=1 AngleXU=0 Radius=1.65
  constraints (14):
    c: Coincident(g0,g-1)
    c: PointOnObject(g0,g-2)
    c: PointOnObject(g1,g-1)
    c: Vertical(g1)
    c: Horizontal(g1,g0)
    c: DistanceY(g0,g0) = 5
    c: Coincident(g2,g0)
    c: Coincident(g2,g1)
    c: Horizontal(g2,g1)
    c: Diameter(g2) = 8
    c: Coincident(g3,g0)
    c: Coincident(g3,g1)
    c: Coincident(g4,g2)
    c: Diameter(g4) = 3.3
FEATURE [PartDesign::Pad] Pad097
  BaseFeature = -> Fillet069
  Direction = (0,0,-1)
  Length = 2.5
  Length2 = 10
  Profile = -> Sketch186
  ReferenceAxis = -> Sketch186 [N_Axis]
  Reversed = true
  Type = 0
FEATURE [PartDesign::Fillet] Fillet070
  Base = -> Pad097 [Edge72]
  BaseFeature = -> Pad097
  Radius = 4
  SupportTransform = false
  UseAllEdges = false
FEATURE [Sketcher::SketchObject] Sketch188
  ExternalGeometry = -> [Fillet070]
  FullyConstrained = true
  MapMode = 5
  Placement = pos=(0,4,0) rot=(1,0,0;1.5708rad)
  Support = -> [Fillet070]
  sketch-geometry (4):
    g0: LineSegment StartX=15 StartY=26.5 StartZ=0 EndX=18 EndY=23.5 EndZ=0
    g1: LineSegment StartX=18 StartY=23.5 StartZ=0 EndX=18 EndY=13.5 EndZ=0
    g2: LineSegment StartX=18 StartY=13.5 StartZ=0 EndX=15 EndY=10.5 EndZ=0
    g3: LineSegment StartX=15 StartY=10.5 StartZ=0 EndX=15 EndY=26.5 EndZ=0
  constraints (12):
    c: PointOnObject(g0,g-3)
    c: Coincident(g1,g0)
    c: Vertical(g1)
    c: Coincident(g2,g1)
    c: PointOnObject(g2,g-3)
    c: Coincident(g3,g2)
    c: Coincident(g3,g0)
    c: Angle(g2,g3) = 0.785398
    c: Angle(g3,g0) = 0.785398
    c: DistanceY(g0,g-3) = 11
    c: DistanceY(g-3,g2) = 8
    c: DistanceX(g2,g1) = 3
FEATURE [PartDesign::Pocket] Pocket084
  BaseFeature = -> Fillet070
  Direction = (0,1,-2e-16)
  Length = 66.5
  Length2 = 5
  Profile = -> Sketch188
  ReferenceAxis = -> Sketch188 [N_Axis]
  Type = 0
FEATURE [PartDesign::Fillet] Fillet073
  Base = -> Pocket084 [Face89]
  BaseFeature = -> Pocket084
  Radius = 1
  SupportTransform = false
  UseAllEdges = false
FEATURE [PartDesign::Fillet] Fillet074
  Base = -> Fillet073 [Edge194,Edge193,Edge132]
  BaseFeature = -> Fillet073
  Radius = 1
  SupportTransform = false
  UseAllEdges = false
FEATURE [Sketcher::SketchObject] Sketch191
  FullyConstrained = true
  MapMode = 5
  Placement = pos=(0,73,0) rot=(0,0.707107,0.707107;3.14159rad)
  Support = -> [Fillet074]
  sketch-geometry (4):
    g0: ArcOfCircle CenterX=-30 CenterY=30 CenterZ=0 NormalX=0 NormalY=0 NormalZ=1 AngleXU=0 Radius=1 StartAngle=-9e-16 EndAngle=3.14159
    g1: ArcOfCircle CenterX=-30 CenterY=10 CenterZ=0 NormalX=0 NormalY=0 NormalZ=1 AngleXU=0 Radius=1 StartAngle=3.14159 EndAngle=6.28319
    g2: LineSegment StartX=-31 StartY=30 StartZ=0 EndX=-31 EndY=10 EndZ=0
    g3: LineSegment StartX=-29 StartY=10 StartZ=0 EndX=-29 EndY=30 EndZ=0
  constraints (10):
    c: Tangent(g0,g2) = -1.5708
    c: Tangent(g2,g1) = -1.5708
    c: Tangent(g1,g3) = -1.5708
    c: Tangent(g3,g0) = -1.5708
    c: Equal(g0,g1)
    c: Vertical(g2)
    c: Diameter(g0) = 2
    c: DistanceY(g1) = 10
    c: DistanceY(g3,g3) = 20
    c: DistanceX(g1) = -30
FEATURE [PartDesign::Pocket] Pocket087
  BaseFeature = -> Fillet074
  Direction = (0,-1,2e-16)
  Length = 2.5
  Length2 = 5
  Profile = -> Sketch191
  ReferenceAxis = -> Sketch191 [N_Axis]
  Type = 0
FEATURE [PartDesign::LinearPattern] LinearPattern003
  BaseFeature = -> Pocket087
  Direction = -> Sketch191 [H_Axis]
  Length = 60
  Occurrences = 10
  Originals = -> [Pocket087]
  Reversed = true
FEATURE [Sketcher::SketchObject] Sketch192
  FullyConstrained = true
  MapMode = 5
  Placement = pos=(0,0,0) rot=(1,0,0;3.14159rad)
  Support = -> [LinearPattern003]
  sketch-geometry (1):
    g0: Circle CenterX=42.5 CenterY=-17.5 CenterZ=0 NormalX=0 NormalY=0 NormalZ=1 AngleXU=0 Radius=1
  constraints (3):
    c: Diameter(g0) = 2
    c: DistanceX(g0) = 42.5
    c: DistanceY(g0) = -17.5
FEATURE [PartDesign::Pocket] Pocket088
  BaseFeature = -> LinearPattern003
  Direction = (0,0,1)
  Length = 2.5
  Length2 = 5
  Profile = -> Sketch192
  ReferenceAxis = -> Sketch192 [N_Axis]
  Type = 0
FEATURE [PartDesign::MultiTransform] MultiTransform001
  BaseFeature = -> Pocket088
  Originals = -> [Pocket088]
  Transformations = -> [LinearPattern004,LinearPattern005]
FEATURE [PartDesign::Body] Body033
  Group = -> [Sketch160,Pad083,Sketch162,Pad085,Sketch169,Pad091,Sketch170,Pocket073,Sketch171,Pocket074,Sketch172,Pad092,Sketch173,Pocket075,Sketch174,Pocket076,Sketch175,Pocket077,Sketch176,Pad093,Sketch182,Pocket081,Sketch183,Pad096,Sketch184,Pocket082,Fillet069,Sketch186,Pad097,Fillet070,Sketch188,Pocket084,Fillet073,Fillet074,Sketch191,Pocket087,LinearPattern003,Sketch192,Pocket088,MultiTransform001,+15 more]
  Origin = -> Origin032
  Tip = -> Pad100
COMPONENT P37 — recipe-attached ("Body034", modeled in this document).
Construction recipe (the document's own serialized feature program — sketch geometry with constraints, then the solid features built on it; lengths are millimeters unless a unit is written):

FEATURE [Sketcher::SketchObject] Sketch164
  FullyConstrained = true
  MapMode = 5
  Support = -> [XY_Plane033]
  sketch-geometry (1):
    g0: Circle CenterX=0 CenterY=0 CenterZ=0 NormalX=0 NormalY=0 NormalZ=1 AngleXU=0 Radius=6.175
  constraints (2):
    c: Coincident(g0,g-1)
    c: Diameter(g0) = 12.35
FEATURE [PartDesign::Pad] Pad087
  Direction = (0,0,1)
  Length = 2
  Length2 = 10
  Profile = -> Sketch164
  ReferenceAxis = -> Sketch164 [N_Axis]
  Type = 0
FEATURE [Sketcher::SketchObject] Sketch165
  FullyConstrained = true
  MapMode = 5
  Placement = pos=(0,0,0) rot=(1,0,0;3.14159rad)
  Support = -> [Pad087]
  sketch-geometry (1):
    g0: Circle CenterX=0 CenterY=0 CenterZ=0 NormalX=0 NormalY=0 NormalZ=1 AngleXU=0 Radius=5.25
  constraints (2):
    c: Coincident(g0,g-1)
    c: Diameter(g0) = 10.5
FEATURE [PartDesign::Pad] Pad088
  BaseFeature = -> Pad087
  Direction = (0,0,-1)
  Length = 14.5
  Length2 = 10
  Profile = -> Sketch165
  ReferenceAxis = -> Sketch165 [N_Axis]
  Type = 0
FEATURE [Sketcher::SketchObject] Sketch166
  FullyConstrained = true
  MapMode = 5
  Placement = pos=(0,0,2) rot=(0,0,1;0rad)
  Support = -> [Pad088]
  sketch-geometry (1):
    g0: Circle CenterX=0 CenterY=0 CenterZ=0 NormalX=0 NormalY=0 NormalZ=1 AngleXU=0 Radius=2.8
  constraints (2):
    c: Coincident(g0,g-1)
    c: Diameter(g0) = 5.6
FEATURE [PartDesign::Pocket] Pocket072
  BaseFeature = -> Pad088
  Direction = (0,0,-1)
  Length = 5
  Length2 = 5
  Profile = -> Sketch166
  ReferenceAxis = -> Sketch166 [N_Axis]
  Type = 0
FEATURE [Sketcher::SketchObject] Sketch167
  FullyConstrained = true
  MapMode = 5
  Placement = pos=(0,0,-14.5) rot=(1,0,0;3.14159rad)
  Support = -> [Pocket072]
  sketch-geometry (4):
    g0: LineSegment StartX=-1.5 StartY=0 StartZ=0 EndX=1.5 EndY=0 EndZ=0
    g1: LineSegment StartX=1.5 StartY=0 StartZ=0 EndX=1.5 EndY=4.5 EndZ=0
    g2: LineSegment StartX=1.5 StartY=4.5 StartZ=0 EndX=-1.5 EndY=4.5 EndZ=0
    g3: LineSegment StartX=-1.5 StartY=4.5 StartZ=0 EndX=-1.5 EndY=0 EndZ=0
  constraints (11):
    c: Coincident(g0,g1)
    c: Coincident(g1,g2)
    c: Coincident(g2,g3)
    c: Coincident(g3,g0)
    c: Horizontal(g0)
    c: Horizontal(g2)
    c: Vertical(g1)
    c: Vertical(g3)
    c: Symmetric(g0,g0,g-1)
    c: DistanceY(g3,g3) = 4.5
    c: DistanceX(g0,g0) = 3
FEATURE [PartDesign::Pad] Pad089
  BaseFeature = -> Pocket072
  Direction = (0,0,-1)
  Length = 10
  Length2 = 10
  Profile = -> Sketch167
  ReferenceAxis = -> Sketch167 [N_Axis]
  Type = 0
FEATURE [Sketcher::SketchObject] Sketch168
  FullyConstrained = true
  MapMode = 5
  Placement = pos=(0,0,-14.5) rot=(1,0,0;3.14159rad)
  Support = -> [Pad089]
  sketch-geometry (7):
    g0: LineSegment StartX=3.89711 StartY=6.75 StartZ=0 EndX=-3.89711 EndY=6.75 EndZ=0
    g1: LineSegment StartX=-3.89711 StartY=6.75 StartZ=0 EndX=-7.79423 EndY=2.9177e-12 EndZ=0
    g2: LineSegment StartX=-7.79423 StartY=2.9177e-12 StartZ=0 EndX=-3.89711 EndY=-6.75 EndZ=0
    g3: LineSegment StartX=-3.89711 StartY=-6.75 StartZ=0 EndX=3.89711 EndY=-6.75 EndZ=0
    g4: LineSegment StartX=3.89711 StartY=-6.75 StartZ=0 EndX=7.79423 EndY=2.3404e-12 EndZ=0
    g5: LineSegment StartX=7.79423 StartY=2.3404e-12 StartZ=0 EndX=3.89711 EndY=6.75 EndZ=0
    g6: Circle CenterX=0 CenterY=0 CenterZ=0 NormalX=0 NormalY=0 NormalZ=1 AngleXU=0 Radius=7.79423
  constraints (16):
    c: Coincident(g0,g1)
    c: Coincident(g1,g2)
    c: Coincident(g2,g3)
    c: Coincident(g3,g4)
    c: Coincident(g4,g5)
    c: Coincident(g5,g0)
    c: Equal(g0, g1-g5) x5
    c: PointOnObject(g0,g6)
    c: PointOnObject(g1,g6)
    c: PointOnObject(g2,g6)
    c: PointOnObject(g3,g6)
    c: PointOnObject(g4,g6)
    c: PointOnObject(g5,g6)
    c: Coincident(g6,g-1)
    c: Horizontal(g0)
    c: DistanceY(g3,g0) = 13.5
FEATURE [PartDesign::Pad] Pad090
  BaseFeature = -> Pad089
  Direction = (0,0,-1)
  Length = 2
  Length2 = 10
  Profile = -> Sketch168
  ReferenceAxis = -> Sketch168 [N_Axis]
  Reversed = true
  Type = 0
FEATURE [PartDesign::Body] Body034
  Group = -> [Sketch164,Pad087,Sketch165,Pad088,Sketch166,Pocket072,Sketch167,Pad089,Sketch168,Pad090]
  Origin = -> Origin033
  Tip = -> Pad090
COMPONENT P38 — recipe-attached ("Body_M3_20mm001", modeled in this document).
Construction recipe (the document's own serialized feature program — sketch geometry with constraints, then the solid features built on it; lengths are millimeters unless a unit is written):

FEATURE [Sketcher::SketchObject] Sketch177
  FullyConstrained = true
  MapMode = 5
  Support = -> [XY_Plane034]
  sketch-geometry (1):
    g0: Circle CenterX=0 CenterY=0 CenterZ=0 NormalX=0 NormalY=0 NormalZ=1 AngleXU=0 Radius=2.675
  constraints (2):
    c: Coincident(g0,g-1)
    c: Diameter(g0) = 5.35
FEATURE [PartDesign::Pad] Pad094
  Direction = (0,0,1)
  Length = 2.9
  Length2 = 10
  Profile = -> Sketch177
  ReferenceAxis = -> Sketch177 [N_Axis]
  Type = 0
FEATURE [Sketcher::SketchObject] Sketch178
  FullyConstrained = true
  MapMode = 5
  Placement = pos=(0,0,2.9) rot=(0,0,1;0rad)
  Support = -> [Pad094]
  sketch-geometry (1):
    g0: Circle CenterX=0 CenterY=0 CenterZ=0 NormalX=0 NormalY=0 NormalZ=1 AngleXU=0 Radius=1.465
  constraints (2):
    c: Coincident(g0,g-1)
    c: Diameter(g0) = 2.93
FEATURE [PartDesign::Pad] Pad095
  BaseFeature = -> Pad094
  Direction = (0,0,1)
  Length = 12
  Length2 = 10
  Profile = -> Sketch178
  ReferenceAxis = -> Sketch178 [N_Axis]
  Type = 0
FEATURE [Sketcher::SketchObject] Sketch179
  FullyConstrained = true
  MapMode = 5
  Placement = pos=(0,0,0) rot=(1,0,0;3.14159rad)
  Support = -> [Pad095]
  sketch-geometry (7):
    g0: LineSegment StartX=1.20378 StartY=0.695 StartZ=0 EndX=0 EndY=1.39 EndZ=0
    g1: LineSegment StartX=0 StartY=1.39 StartZ=0 EndX=-1.20378 EndY=0.695 EndZ=0
    g2: LineSegment StartX=-1.20378 StartY=0.695 StartZ=0 EndX=-1.20378 EndY=-0.695 EndZ=0
    g3: LineSegment StartX=-1.20378 StartY=-0.695 StartZ=0 EndX=1.122e-12 EndY=-1.39 EndZ=0
    g4: LineSegment StartX=1.122e-12 StartY=-1.39 StartZ=0 EndX=1.20378 EndY=-0.695 EndZ=0
    g5: LineSegment StartX=1.20378 StartY=-0.695 StartZ=0 EndX=1.20378 EndY=0.695 EndZ=0
    g6: Circle CenterX=0 CenterY=0 CenterZ=0 NormalX=0 NormalY=0 NormalZ=1 AngleXU=0 Radius=1.39
  constraints (16):
    c: Coincident(g0,g1)
    c: Coincident(g1,g2)
    c: Coincident(g2,g3)
    c: Coincident(g3,g4)
    c: Coincident(g4,g5)
    c: Coincident(g5,g0)
    c: Equal(g0, g1-g5) x5
    c: PointOnObject(g0,g6)
    c: PointOnObject(g1,g6)
    c: PointOnObject(g2,g6)
    c: PointOnObject(g3,g6)
    c: PointOnObject(g4,g6)
    c: PointOnObject(g5,g6)
    c: Coincident(g6,g-1)
    c: Vertical(g6,g0)
    c: Diameter(g6) = 2.78
FEATURE [PartDesign::Pocket] Pocket078
  BaseFeature = -> Pad095
  Direction = (0,0,1)
  Length = 1.94
  Length2 = 5
  Profile = -> Sketch179
  ReferenceAxis = -> Sketch179 [N_Axis]
  Type = 0
FEATURE [PartDesign::Body] Body035  label="Body_M3_20mm001"
  Group = -> [Sketch177,Pad094,Sketch178,Pad095,Sketch179,Pocket078]
  Origin = -> Origin034
  Tip = -> Pocket078
COMPONENT P39 — geometry summary ("40cm_2020_extrusion-01"; no construction recipe available for this part):
  bounding box: 400.0 x 20.0 x 20.0 mm
  tessellated surface: 800 triangles
  volume: 69223 mm^3 (43% of its bounding box)
  symmetry: 2-fold rotationally symmetric about the x axis; 4-fold rotationally symmetric about the y axis; 2-fold rotationally symmetric about the z axis; mirror-symmetric across its x mid-plane, y mid-plane, z mid-plane
COMPONENT P40 — geometry summary ("40cm_2020_extrusion-02"; no construction recipe available for this part):
  bounding box: 400.0 x 20.0 x 20.0 mm
  tessellated surface: 800 triangles
  volume: 69223 mm^3 (43% of its bounding box)
  symmetry: 2-fold rotationally symmetric about the x axis; 4-fold rotationally symmetric about the y axis; 2-fold rotationally symmetric about the z axis; mirror-symmetric across its x mid-plane, y mid-plane, z mid-plane
COMPONENT P41 — geometry summary ("40cm_2020_extrusion-03"; no construction recipe available for this part):
  bounding box: 400.0 x 20.0 x 20.0 mm
  tessellated surface: 800 triangles
  volume: 69223 mm^3 (43% of its bounding box)
  symmetry: 2-fold rotationally symmetric about the x axis; 4-fold rotationally symmetric about the y axis; 2-fold rotationally symmetric about the z axis; mirror-symmetric across its x mid-plane, y mid-plane, z mid-plane
COMPONENT P42 — geometry summary ("40cm_2020_extrusion-04"; no construction recipe available for this part):
  bounding box: 400.0 x 20.0 x 20.0 mm
  tessellated surface: 800 triangles
  volume: 69223 mm^3 (43% of its bounding box)
  symmetry: 2-fold rotationally symmetric about the x axis; 4-fold rotationally symmetric about the y axis; 2-fold rotationally symmetric about the z axis; mirror-symmetric across its x mid-plane, y mid-plane, z mid-plane
COMPONENT P43 — geometry summary ("40cm_2020_extrusion-05"; no construction recipe available for this part):
  bounding box: 400.0 x 20.0 x 20.0 mm
  tessellated surface: 800 triangles
  volume: 69223 mm^3 (43% of its bounding box)
  symmetry: 2-fold rotationally symmetric about the x axis; 4-fold rotationally symmetric about the y axis; 2-fold rotationally symmetric about the z axis; mirror-symmetric across its x mid-plane, y mid-plane, z mid-plane
COMPONENT P44 — recipe-attached ("food_dish_left", a linked part whose construction recipe lives in a companion FreeCAD document of the same project; that document's serialized recipe follows).
Construction recipe (the companion document, serialized — sketch geometry with constraints, then the solid features built on it; lengths are millimeters unless a unit is written):

FCSTD DOCUMENT  (FreeCAD 0.20R29410 (Git))
Label: food_dish
License: All rights reserved
LicenseURL: http://en.wikipedia.org/wiki/All_rights_reserved
objects: Sketcher::SketchObject×1, PartDesign::Revolution×1, PartDesign::Body×1
note: 4 computed .brp shape members not serialized (recipe doc carries the construction recipe); baked Part::Feature solids carry a one-line shape summary decoded from their .brp

FEATURE [Sketcher::SketchObject] Sketch
  FullyConstrained = true
  MapMode = 5
  Placement = pos=(0,0,0) rot=(1,0,0;1.5708rad)
  Support = -> [XZ_Plane]
  sketch-geometry (8):
    g0: LineSegment StartX=0 StartY=0 StartZ=0 EndX=65 EndY=0 EndZ=0
    g1: LineSegment StartX=0 StartY=0 StartZ=0 EndX=0 EndY=1 EndZ=0
    g2: LineSegment StartX=0 StartY=1 StartZ=0 EndX=64.3618 EndY=1 EndZ=0
    g3: LineSegment StartX=65 StartY=0 StartZ=0 EndX=78 EndY=28 EndZ=0
    g4: LineSegment StartX=78 StartY=28 StartZ=0 EndX=76.8975 EndY=28 EndZ=0
    g5: LineSegment StartX=76.8975 StartY=28 StartZ=0 EndX=64.3618 EndY=1 EndZ=0
    g6: GeomPoint X=77.8045 Y=27.5789 Z=0
    g7: LineSegment StartX=76.8975 StartY=28 StartZ=0 EndX=77.8045 EndY=27.5789 EndZ=0
  constraints (21):
    c: Coincident(g0,g-1)
    c: PointOnObject(g0,g-1)
    c: DistanceX(g0) = 65
    c: Coincident(g1,g0)
    c: PointOnObject(g1,g-2)
    c: Coincident(g2,g1)
    c: Horizontal(g2)
    c: DistanceY(g1) = 1
    c: Coincident(g3,g0)
    c: Coincident(g4,g3)
    c: Coincident(g5,g4)
    c: Coincident(g5,g2)
    c: Parallel(g5,g3)
    c: Horizontal(g4)
    c: DistanceY(g3) = 28
    c: PointOnObject(g6,g3)
    c: Coincident(g7,g4)
    c: Coincident(g7,g6)
    c: Perpendicular(g5,g7)
    c: DistanceX(g3) = 78
    c: Distance(g7) = 1
FEATURE [PartDesign::Revolution] Revolution  label="food_dish"
  Angle = 360
  Axis = (-3e-16,3e-16,1)
  Base = (0,0,0)
  Placement = pos=(0,0,0) rot=(1,0,0;1.5708rad)
  Profile = -> Sketch
  ReferenceAxis = -> Z_Axis
  Reversed = true
FEATURE [PartDesign::Body] Body
  Group = -> [Sketch,Revolution]
  Origin = -> Origin
  Tip = -> Revolution
COMPONENT P45 — same part as P44; its construction recipe is shown at P44.
COMPONENT P46 — geometry summary ("40_cm_2020_vertical-left"; no construction recipe available for this part):
  bounding box: 400.0 x 20.0 x 20.0 mm
  tessellated surface: 800 triangles
  volume: 69223 mm^3 (43% of its bounding box)
  symmetry: 2-fold rotationally symmetric about the x axis; 4-fold rotationally symmetric about the y axis; 2-fold rotationally symmetric about the z axis; mirror-symmetric across its x mid-plane, y mid-plane, z mid-plane
COMPONENT P47 — geometry summary ("orthogonal-left-front"; no construction recipe available for this part):
  bounding box: 20.9 x 20.9 x 20.0 mm
  tessellated surface: 2,468 triangles
  volume: 1939 mm^3 (22% of its bounding box)
  symmetry: mirror-symmetric across its z mid-plane
COMPONENT P48 — geometry summary ("orthogonal-left-back"; no construction recipe available for this part):
  bounding box: 20.9 x 20.9 x 20.0 mm
  tessellated surface: 2,468 triangles
  volume: 1939 mm^3 (22% of its bounding box)
  symmetry: mirror-symmetric across its z mid-plane
COMPONENT P49 — geometry summary ("40cm_2020_extrusion-06"; no construction recipe available for this part):
  bounding box: 400.0 x 20.0 x 20.0 mm
  tessellated surface: 800 triangles
  volume: 69223 mm^3 (43% of its bounding box)
  symmetry: 2-fold rotationally symmetric about the x axis; 4-fold rotationally symmetric about the y axis; 2-fold rotationally symmetric about the z axis; mirror-symmetric across its x mid-plane, y mid-plane, z mid-plane
COMPONENT P50 — geometry summary ("orthogonal-right-front"; no construction recipe available for this part):
  bounding box: 20.9 x 20.9 x 20.0 mm
  tessellated surface: 2,468 triangles
  volume: 1939 mm^3 (22% of its bounding box)
  symmetry: mirror-symmetric across its z mid-plane
COMPONENT P51 — geometry summary ("40cm_2020_extrusion-007"; no construction recipe available for this part):
  bounding box: 400.0 x 20.0 x 20.0 mm
  tessellated surface: 800 triangles
  volume: 69223 mm^3 (43% of its bounding box)
  symmetry: 2-fold rotationally symmetric about the x axis; 4-fold rotationally symmetric about the y axis; 2-fold rotationally symmetric about the z axis; mirror-symmetric across its x mid-plane, y mid-plane, z mid-plane
PROVENANCE & LICENSES
A FreeCAD (.FCStd) document from a public repository crawl; recipes are the document's own serialized feature recipes (and, for linked parts, companion documents' recipes).
License: mit.
